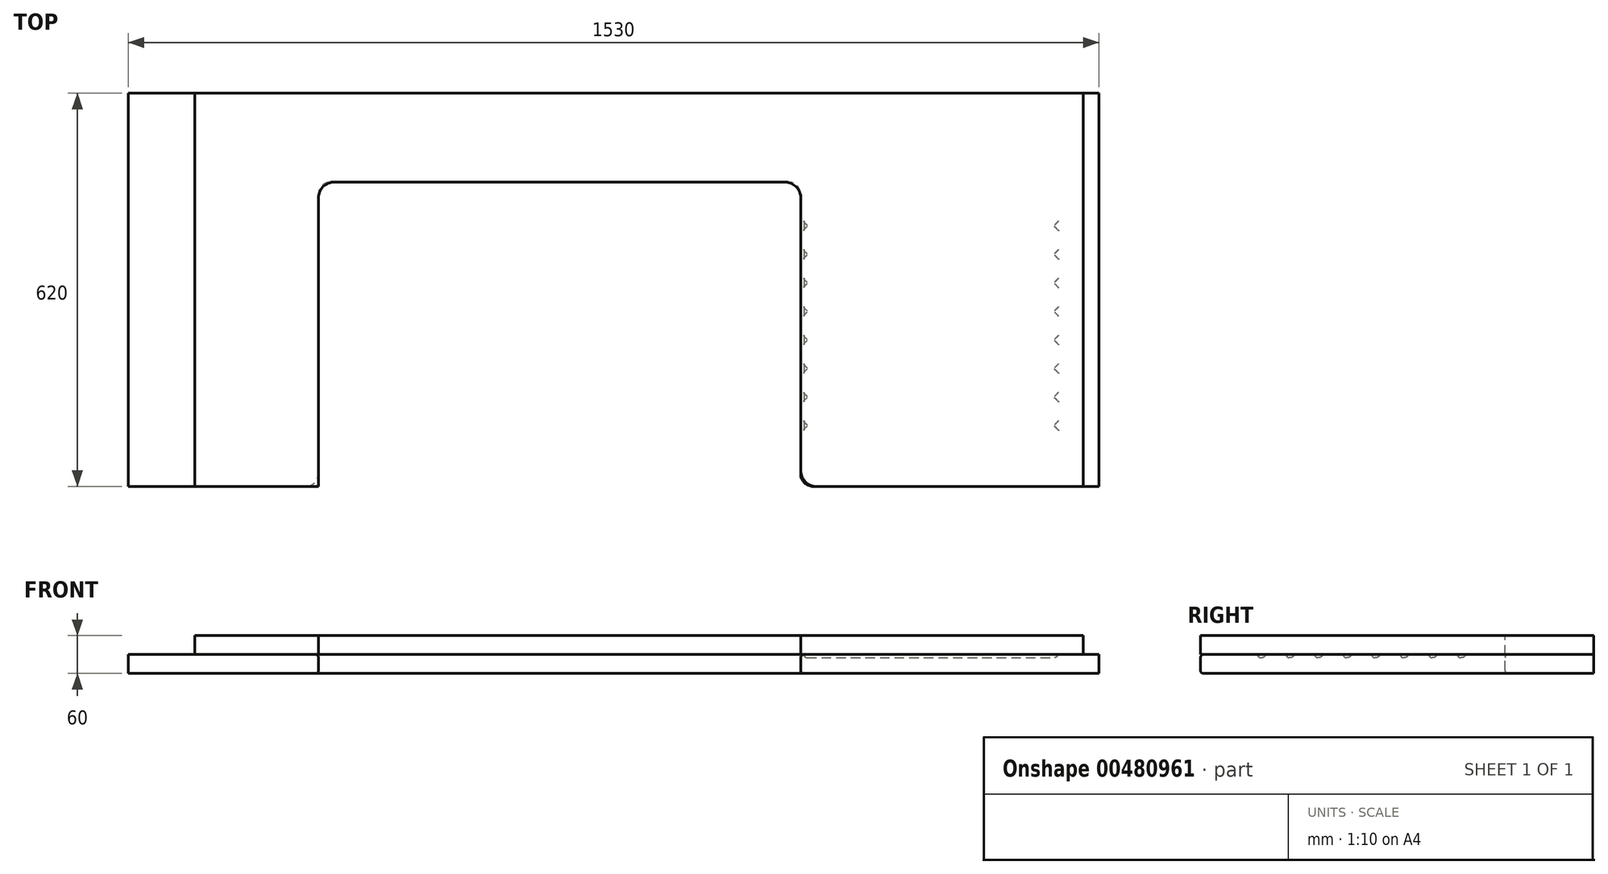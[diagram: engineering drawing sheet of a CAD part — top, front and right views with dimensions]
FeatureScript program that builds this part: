
annotation { "Feature Type Name" : "Feature", "Feature Type Description" : "" }
export const myFeature = defineFeature(function(context is Context, id is Id, definition is map)
    precondition{}
    {
        {
            var Q0;
            Q0=qCreatedBy(makeId("Top.planeOp"),FACE);
            var sketch = newSketch(context, id + "F0", { "sketchPlane" : qUnion([Q0])});
            skLineSegment(sketch, "E0.bottom", {"start": v(1945, 1810) * mm, "end": v(-1945, 1810) * mm});
            skLineSegment(sketch, "E0.top", {"start": v(1945, -1810) * mm, "end": v(-1945, -1810) * mm});
            skLineSegment(sketch, "E0.left", {"start": v(1945, 1810) * mm, "end": v(1945, -1810) * mm});
            skLineSegment(sketch, "E0.right", {"start": v(-1945, 1810) * mm, "end": v(-1945, -1810) * mm});
            skPoint(sketch, "E0.middle", {"position": v(0, 0) * mm});
            skLineSegment(sketch, "E1", {"start": v(1945, 1810) * mm, "end": v(1945, 45) * mm});
            skLineSegment(sketch, "E2.right", {"start": v(1945, 1810) * mm, "end": v(1945, 1158) * mm});
            skLineSegment(sketch, "E3.bottom", {"start": v(1945, 1810) * mm, "end": v(1285, 1810) * mm});
            skLineSegment(sketch, "E4.bottom", {"start": v(1945, 730) * mm, "end": v(1300, 730) * mm});
            skLineSegment(sketch, "E4.top", {"start": v(1945, 135) * mm, "end": v(1300, 135) * mm});
            skLineSegment(sketch, "E4.left", {"start": v(1945, 730) * mm, "end": v(1945, 135) * mm});
            skLineSegment(sketch, "E4.right", {"start": v(1300, 730) * mm, "end": v(1300, 135) * mm});
            skPoint(sketch, "E5.endSnap0", {"position": v(0, 1810) * mm});
            skLineSegment(sketch, "E6.bottom", {"start": v(-315, 1810) * mm, "end": v(485, 1810) * mm});
            skLineSegment(sketch, "E6.top", {"start": v(-315, 1250) * mm, "end": v(485, 1250) * mm});
            skLineSegment(sketch, "E6.left", {"start": v(-315, 1810) * mm, "end": v(-315, 1250) * mm});
            skLineSegment(sketch, "E6.right", {"start": v(485, 1810) * mm, "end": v(485, 1250) * mm});
            skLineSegment(sketch, "E7.bottom", {"start": v(485, 1810) * mm, "end": v(1085, 1810) * mm});
            skLineSegment(sketch, "E7.top", {"start": v(485, 1250) * mm, "end": v(1085, 1250) * mm});
            skLineSegment(sketch, "E7.right", {"start": v(1085, 1810) * mm, "end": v(1085, 1250) * mm});
            skLineSegment(sketch, "E8", {"start": v(1285, 1250) * mm, "end": v(1285, 780) * mm});
            skLineSegment(sketch, "E9", {"start": v(1285, 780) * mm, "end": v(1945, 780) * mm});
            skLineSegment(sketch, "E10", {"start": v(1285, 1250) * mm, "end": v(1285, 1810) * mm});
            skLineSegment(sketch, "E11", {"start": v(1285, 1680) * mm, "end": v(1845, 1680) * mm});
            skLineSegment(sketch, "E12.bottom", {"start": v(1285, 1250) * mm, "end": v(1215, 1250) * mm});
            skLineSegment(sketch, "E12.top", {"start": v(1285, 1810) * mm, "end": v(1215, 1810) * mm});
            skLineSegment(sketch, "E12.right", {"start": v(1215, 1250) * mm, "end": v(1215, 1810) * mm});
            skLineSegment(sketch, "E13.left", {"start": v(1215, 1810) * mm, "end": v(1215, 1250) * mm});
            skLineSegment(sketch, "E14", {"start": v(1215, 1250) * mm, "end": v(1085, 1250) * mm});
            skLineSegment(sketch, "E15.bottom", {"start": v(-315, 1250) * mm, "end": v(-715, 1250) * mm});
            skLineSegment(sketch, "E15.top", {"start": v(-315, 1810) * mm, "end": v(-715, 1810) * mm});
            skLineSegment(sketch, "E15.left", {"start": v(-315, 1250) * mm, "end": v(-315, 1810) * mm});
            skLineSegment(sketch, "E15.right", {"start": v(-715, 1250) * mm, "end": v(-715, 1810) * mm});
            skLineSegment(sketch, "E16.bottom", {"start": v(-1945, 1680) * mm, "end": v(-1385, 1680) * mm});
            skLineSegment(sketch, "E16.top", {"start": v(-1945, 680) * mm, "end": v(-1385, 680) * mm});
            skLineSegment(sketch, "E16.left", {"start": v(-1945, 1680) * mm, "end": v(-1945, 680) * mm});
            skLineSegment(sketch, "E16.right", {"start": v(-1385, 1680) * mm, "end": v(-1385, 680) * mm});
            skLineSegment(sketch, "E17.top", {"start": v(-1945, -220) * mm, "end": v(-1385, -220) * mm});
            skLineSegment(sketch, "E17.left", {"start": v(-1945, 680) * mm, "end": v(-1945, -220) * mm});
            skLineSegment(sketch, "E17.right", {"start": v(-1385, 680) * mm, "end": v(-1385, -220) * mm});
            skLineSegment(sketch, "E18.bottom", {"start": v(-1385, 1250) * mm, "end": v(-1315, 1250) * mm});
            skLineSegment(sketch, "E18.top", {"start": v(-1385, 1810) * mm, "end": v(-1315, 1810) * mm});
            skLineSegment(sketch, "E18.left", {"start": v(-1385, 1250) * mm, "end": v(-1385, 1810) * mm});
            skLineSegment(sketch, "E18.right", {"start": v(-1315, 1250) * mm, "end": v(-1315, 1810) * mm});
            skLineSegment(sketch, "E19.bottom", {"start": v(-715, 1250) * mm, "end": v(-1315, 1250) * mm});
            skLineSegment(sketch, "E19.top", {"start": v(-715, 1810) * mm, "end": v(-1315, 1810) * mm});
            skLineSegment(sketch, "E20.bottom", {"start": v(-1385, -220) * mm, "end": v(-1945, -220) * mm});
            skLineSegment(sketch, "E20.top", {"start": v(-1385, -1220) * mm, "end": v(-1945, -1220) * mm});
            skLineSegment(sketch, "E20.left", {"start": v(-1385, -220) * mm, "end": v(-1385, -1220) * mm});
            skLineSegment(sketch, "E20.right", {"start": v(-1945, -220) * mm, "end": v(-1945, -1220) * mm});
            skLineSegment(sketch, "E21.top", {"start": v(-1385, -1720) * mm, "end": v(-1945, -1720) * mm});
            skLineSegment(sketch, "E21.left", {"start": v(-1385, -1220) * mm, "end": v(-1385, -1720) * mm});
            skLineSegment(sketch, "E21.right", {"start": v(-1945, -1220) * mm, "end": v(-1945, -1720) * mm});
            skLineSegment(sketch, "E22.bottom", {"start": v(-385, 250) * mm, "end": v(175, 250) * mm});
            skLineSegment(sketch, "E22.top", {"start": v(-385, -650) * mm, "end": v(175, -650) * mm});
            skLineSegment(sketch, "E22.left", {"start": v(-385, 250) * mm, "end": v(-385, -650) * mm});
            skLineSegment(sketch, "E22.right", {"start": v(175, 250) * mm, "end": v(175, -650) * mm});
            skLineSegment(sketch, "E23.top", {"start": v(175, -260) * mm, "end": v(275, -260) * mm});
            skLineSegment(sketch, "E23.left", {"start": v(175, 250) * mm, "end": v(175, -260) * mm});
            skLineSegment(sketch, "E24.bottom", {"start": v(275, -260) * mm, "end": v(175, -260) * mm});
            skLineSegment(sketch, "E24.right", {"start": v(175, -260) * mm, "end": v(175, -650) * mm});
            skLineSegment(sketch, "E25.bottom", {"start": v(7324.8, -1561.68) * mm, "end": v(7884.8, -1561.68) * mm});
            skLineSegment(sketch, "E25.top", {"start": v(7324.8, -691.68) * mm, "end": v(7884.8, -691.68) * mm});
            skLineSegment(sketch, "E25.left", {"start": v(7324.8, -1561.68) * mm, "end": v(7324.8, -691.68) * mm});
            skLineSegment(sketch, "E25.right", {"start": v(7884.8, -1561.68) * mm, "end": v(7884.8, -691.68) * mm});
            skLineSegment(sketch, "E26.left", {"start": v(7324.8, -161.68) * mm, "end": v(7324.8, 738.32) * mm});
            skLineSegment(sketch, "E27", {"start": v(7324.8, -1561.68) * mm, "end": v(7324.8, 813.32) * mm});
            skPoint(sketch, "E26.top.end.orphan", {"position": v(7884.8, 608.32) * mm});
            skLineSegment(sketch, "E28.bottom", {"start": v(7324.8, -161.68) * mm, "end": v(7724.8, -161.68) * mm});
            skLineSegment(sketch, "E28.top", {"start": v(7324.8, 738.32) * mm, "end": v(7724.8, 738.32) * mm});
            skLineSegment(sketch, "E28.right", {"start": v(7724.8, -161.68) * mm, "end": v(7724.8, 738.32) * mm});
            skLineSegment(sketch, "E29", {"start": v(-1015, 1810) * mm, "end": v(-1015, 1589) * mm, "construction": true});
            skLineSegment(sketch, "E30.bottom", {"start": v(-310, 2102.18) * mm, "end": v(460, 2102.18) * mm});
            skLineSegment(sketch, "E30.top", {"start": v(-310, 1971.27) * mm, "end": v(460, 1971.27) * mm});
            skLineSegment(sketch, "E30.left", {"start": v(-310, 2102.18) * mm, "end": v(-310, 1971.27) * mm});
            skLineSegment(sketch, "E30.right", {"start": v(460, 2102.18) * mm, "end": v(460, 1971.27) * mm});
            skLineSegment(sketch, "E31.top", {"start": v(-310, 1810) * mm, "end": v(-1945, 1810) * mm});
            skLineSegment(sketch, "E32.bottom", {"start": v(485, 1810) * mm, "end": v(635, 1810) * mm});
            skLineSegment(sketch, "E32.top", {"start": v(485, 1250) * mm, "end": v(635, 1250) * mm});
            skLineSegment(sketch, "E33", {"start": v(1845, 1680) * mm, "end": v(1845, 780) * mm});
            skLineSegment(sketch, "E34.bottom", {"start": v(485, 1810) * mm, "end": v(562.5, 1810) * mm});
            skLineSegment(sketch, "E34.top", {"start": v(485, 1250) * mm, "end": v(785, 1250) * mm});
            skPoint(sketch, "E35.start.orphan", {"position": v(1150, 1250) * mm});
            skLineSegment(sketch, "E36.bottom", {"start": v(1085, 1810) * mm, "end": v(1185, 1810) * mm});
            skLineSegment(sketch, "E36.top", {"start": v(1085, 1250) * mm, "end": v(1185, 1250) * mm});
            skLineSegment(sketch, "E36.right", {"start": v(1185, 1810) * mm, "end": v(1185, 1250) * mm});
            skLineSegment(sketch, "E37", {"start": v(785, 1810) * mm, "end": v(785, 1670.24) * mm, "construction": true});
            skLineSegment(sketch, "E38.bottom", {"start": v(7324.8, -1411.68) * mm, "end": v(7884.8, -1411.68) * mm});
            skLineSegment(sketch, "E38.left", {"start": v(7324.8, -1411.68) * mm, "end": v(7324.8, -691.68) * mm});
            skLineSegment(sketch, "E38.right", {"start": v(7884.8, -1411.68) * mm, "end": v(7884.8, -691.68) * mm});
            skLineSegment(sketch, "E39.bottom", {"start": v(7324.8, -691.68) * mm, "end": v(7909.99, -691.68) * mm});
            skLineSegment(sketch, "E39.top", {"start": v(7324.8, -651.68) * mm, "end": v(7909.99, -651.68) * mm});
            skLineSegment(sketch, "E39.left", {"start": v(7324.8, -691.68) * mm, "end": v(7324.8, -651.68) * mm});
            skLineSegment(sketch, "E39.right", {"start": v(7909.99, -691.68) * mm, "end": v(7909.99, -651.68) * mm});
            skLineSegment(sketch, "E40.bottom", {"start": v(7884.8, -1411.68) * mm, "end": v(7324.8, -1411.68) * mm});
            skLineSegment(sketch, "E40.top", {"start": v(7884.8, -916.68) * mm, "end": v(7324.8, -916.68) * mm});
            skLineSegment(sketch, "E40.left", {"start": v(7884.8, -1411.68) * mm, "end": v(7884.8, -916.68) * mm});
            skLineSegment(sketch, "E40.right", {"start": v(7324.8, -1411.68) * mm, "end": v(7324.8, -916.68) * mm});
            skLineSegment(sketch, "E41.bottom", {"start": v(7324.8, -916.68) * mm, "end": v(7884.8, -916.68) * mm});
            skLineSegment(sketch, "E41.top", {"start": v(7324.8, -716.68) * mm, "end": v(7884.8, -716.68) * mm});
            skLineSegment(sketch, "E41.left", {"start": v(7324.8, -916.68) * mm, "end": v(7324.8, -716.68) * mm});
            skLineSegment(sketch, "E41.right", {"start": v(7884.8, -916.68) * mm, "end": v(7884.8, -716.68) * mm});
            skLineSegment(sketch, "E42.left", {"start": v(-385, 250) * mm, "end": v(-385, 269) * mm});
            skLineSegment(sketch, "E43.top", {"start": v(1285, 761) * mm, "end": v(1945, 761) * mm});
            skLineSegment(sketch, "E43.left", {"start": v(1285, 780) * mm, "end": v(1285, 761) * mm});
            skLineSegment(sketch, "E43.right", {"start": v(1945, 780) * mm, "end": v(1945, 761) * mm});
            skLineSegment(sketch, "E44.bottom", {"start": v(-1945, -1720) * mm, "end": v(-1385, -1720) * mm});
            skLineSegment(sketch, "E44.left", {"start": v(-1945, -1720) * mm, "end": v(-1945, -1739) * mm});
            skLineSegment(sketch, "E45.bottom", {"start": v(-385, 250) * mm, "end": v(-285, 250) * mm});
            skLineSegment(sketch, "E45.top", {"start": v(-355, 300) * mm, "end": v(-285, 300) * mm});
            skLineSegment(sketch, "E45.left", {"start": v(-385, 250) * mm, "end": v(-385, 270) * mm});
            skLineSegment(sketch, "E45.right", {"start": v(-285, 250) * mm, "end": v(-285, 300) * mm});
            skPoint(sketch, "E46.visualSharp", {"position": v(-385, 300) * mm});
            skArc(sketch, "E46.filletArc", {"start": v(-355, 300) * mm, "mid": v(-376.21, 291.21) * mm, "end": v(-385, 270) * mm});
            skLineSegment(sketch, "E47.left", {"start": v(-285, 300) * mm, "end": v(-285, 281) * mm});
            skPoint(sketch, "E47.right.end.orphan", {"position": v(344, 281) * mm});
            skLineSegment(sketch, "E48.bottom", {"start": v(-285, 300) * mm, "end": v(175, 300) * mm});
            skLineSegment(sketch, "E48.top", {"start": v(-285, 281) * mm, "end": v(175, 281) * mm});
            skLineSegment(sketch, "E48.right", {"start": v(175, 300) * mm, "end": v(175, 281) * mm});
            skLineSegment(sketch, "E49", {"start": v(175, 250) * mm, "end": v(175, 300) * mm});
            skPoint(sketch, "E50.right.start.orphan", {"position": v(344, 269) * mm});
            skPoint(sketch, "E51.end.orphan", {"position": v(275, -264.2) * mm});
            skPoint(sketch, "E51.start.orphan", {"position": v(275, 300) * mm});
            skLineSegment(sketch, "E52.bottom", {"start": v(175, 300) * mm, "end": v(275, 300) * mm});
            skLineSegment(sketch, "E52.left", {"start": v(175, 300) * mm, "end": v(175, -260) * mm});
            skLineSegment(sketch, "E52.right", {"start": v(275, 300) * mm, "end": v(275, -260) * mm});
            skLineSegment(sketch, "E53.bottom", {"start": v(-385, -650) * mm, "end": v(-285, -650) * mm});
            skLineSegment(sketch, "E53.top", {"start": v(-355, -700) * mm, "end": v(-285, -700) * mm});
            skLineSegment(sketch, "E53.left", {"start": v(-385, -650) * mm, "end": v(-385, -670) * mm});
            skLineSegment(sketch, "E53.right", {"start": v(-285, -650) * mm, "end": v(-285, -700) * mm});
            skPoint(sketch, "E54.visualSharp", {"position": v(-385, -700) * mm});
            skArc(sketch, "E54.filletArc", {"start": v(-385, -670) * mm, "mid": v(-376.21, -691.21) * mm, "end": v(-355, -700) * mm});
            skLineSegment(sketch, "E55.bottom", {"start": v(-285, -700) * mm, "end": v(275, -700) * mm});
            skLineSegment(sketch, "E55.top", {"start": v(-285, -681) * mm, "end": v(175, -681) * mm});
            skLineSegment(sketch, "E55.left", {"start": v(-285, -700) * mm, "end": v(-285, -681) * mm});
            skLineSegment(sketch, "E55.right", {"start": v(275, -700) * mm, "end": v(275, -681) * mm});
            skLineSegment(sketch, "E56.top", {"start": v(275, -700) * mm, "end": v(175, -700) * mm});
            skLineSegment(sketch, "E56.left", {"start": v(275, -260) * mm, "end": v(275, -700) * mm});
            skLineSegment(sketch, "E56.right", {"start": v(175, -260) * mm, "end": v(175, -700) * mm});
            skLineSegment(sketch, "E57.bottom", {"start": v(275, 300) * mm, "end": v(294, 300) * mm});
            skLineSegment(sketch, "E57.top", {"start": v(275, -700) * mm, "end": v(294, -700) * mm});
            skLineSegment(sketch, "E57.left", {"start": v(275, 300) * mm, "end": v(275, -700) * mm});
            skLineSegment(sketch, "E57.right", {"start": v(294, 300) * mm, "end": v(294, -700) * mm});
            skLineSegment(sketch, "E58.bottom", {"start": v(-1945, -1770) * mm, "end": v(-1485, -1770) * mm});
            skLineSegment(sketch, "E58.top", {"start": v(-1945, -1751) * mm, "end": v(-1485, -1751) * mm});
            skLineSegment(sketch, "E58.left", {"start": v(-1945, -1770) * mm, "end": v(-1945, -1751) * mm});
            skLineSegment(sketch, "E58.right", {"start": v(-1485, -1770) * mm, "end": v(-1485, -1751) * mm});
            skLineSegment(sketch, "E59.bottom", {"start": v(-1385, -1720) * mm, "end": v(-1485, -1720) * mm});
            skLineSegment(sketch, "E59.top", {"start": v(-1415, -1770) * mm, "end": v(-1485, -1770) * mm});
            skLineSegment(sketch, "E59.left", {"start": v(-1385, -1720) * mm, "end": v(-1385, -1740) * mm});
            skLineSegment(sketch, "E59.right", {"start": v(-1485, -1720) * mm, "end": v(-1485, -1770) * mm});
            skPoint(sketch, "E60.visualSharp", {"position": v(-1385, -1770) * mm});
            skArc(sketch, "E60.filletArc", {"start": v(-1415, -1770) * mm, "mid": v(-1393.79, -1761.21) * mm, "end": v(-1385, -1740) * mm});
            skLineSegment(sketch, "E61.left", {"start": v(7324.8, 738.32) * mm, "end": v(7324.8, 378.32) * mm});
            skLineSegment(sketch, "E61.right", {"start": v(7724.8, 738.32) * mm, "end": v(7724.8, 288.32) * mm});
            skLineSegment(sketch, "E62.left", {"start": v(7724.8, -191.68) * mm, "end": v(7724.8, 508.32) * mm});
            skLineSegment(sketch, "E62.right", {"start": v(7324.8, -191.68) * mm, "end": v(7324.8, 508.32) * mm});
            skLineSegment(sketch, "E63", {"start": v(-1945, 230) * mm, "end": v(-1763.05, 230) * mm});
            skLineSegment(sketch, "E64.bottom", {"start": v(7324.8, -136.68) * mm, "end": v(7689.8, -136.68) * mm});
            skLineSegment(sketch, "E64.top", {"start": v(7324.8, 623.32) * mm, "end": v(7689.8, 623.32) * mm});
            skLineSegment(sketch, "E64.left", {"start": v(7324.8, -136.68) * mm, "end": v(7324.8, 623.32) * mm});
            skLineSegment(sketch, "E64.right", {"start": v(7689.8, -136.68) * mm, "end": v(7689.8, 623.32) * mm});
            skPoint(sketch, "E65.oppositeSnap0", {"position": v(7507.3, 623.32) * mm});
            skLineSegment(sketch, "E65.bottom", {"start": v(7407.3, 623.32) * mm, "end": v(7507.3, 623.32) * mm});
            skLineSegment(sketch, "E65.top", {"start": v(7407.3, 723.32) * mm, "end": v(7507.3, 723.32) * mm});
            skLineSegment(sketch, "E65.left", {"start": v(7407.3, 623.32) * mm, "end": v(7407.3, 723.32) * mm});
            skLineSegment(sketch, "E65.right", {"start": v(7507.3, 623.32) * mm, "end": v(7507.3, 723.32) * mm});
            skSolve(sketch);
        }
        {
            var Q0;
            Q0=qCreatedBy(makeId("Top.planeOp"),FACE);
            var sketch = newSketch(context, id + "F1", { "sketchPlane" : qUnion([Q0])});
            skLineSegment(sketch, "E66.bottom", {"start": v(1945, 1810) * mm, "end": v(1845, 1810) * mm});
            skLineSegment(sketch, "E66.top", {"start": v(1945, 780) * mm, "end": v(1845, 780) * mm});
            skLineSegment(sketch, "E66.left", {"start": v(1945, 1810) * mm, "end": v(1945, 780) * mm});
            skLineSegment(sketch, "E67", {"start": v(1845, 780) * mm, "end": v(1845, 1810) * mm});
            skLineSegment(sketch, "E68", {"start": v(1845, 1810) * mm, "end": v(1235, 1810) * mm});
            skLineSegment(sketch, "E69", {"start": v(1235, 1810) * mm, "end": v(1235, 1510) * mm});
            skLineSegment(sketch, "E70", {"start": v(1235, 1510) * mm, "end": v(1235, 1510) * mm});
            skLineSegment(sketch, "E71", {"start": v(1545, 1510) * mm, "end": v(1545, 1510) * mm});
            skLineSegment(sketch, "E72", {"start": v(1545, 1510) * mm, "end": v(1845, 1510) * mm});
            skLineSegment(sketch, "E73.bottom", {"start": v(1845, 1510) * mm, "end": v(1545, 1510) * mm});
            skLineSegment(sketch, "E73.top", {"start": v(1845, 1480) * mm, "end": v(1545, 1480) * mm});
            skLineSegment(sketch, "E73.left", {"start": v(1845, 1510) * mm, "end": v(1845, 1480) * mm});
            skLineSegment(sketch, "E73.right", {"start": v(1545, 1510) * mm, "end": v(1545, 1480) * mm});
            skLineSegment(sketch, "E74.bottom", {"start": v(1235, 1810) * mm, "end": v(635, 1810) * mm});
            skLineSegment(sketch, "E74.top", {"start": v(1235, 1510) * mm, "end": v(635, 1510) * mm});
            skLineSegment(sketch, "E74.right", {"start": v(635, 1810) * mm, "end": v(635, 1510) * mm});
            skLineSegment(sketch, "E75.bottom", {"start": v(1235, 1810) * mm, "end": v(970, 1810) * mm});
            skLineSegment(sketch, "E75.top", {"start": v(1235, 1510) * mm, "end": v(970, 1510) * mm});
            skLineSegment(sketch, "E76.bottom", {"start": v(-495, 1810) * mm, "end": v(-1215, 1810) * mm});
            skLineSegment(sketch, "E76.top", {"start": v(-495, 1510) * mm, "end": v(-1215, 1510) * mm});
            skLineSegment(sketch, "E76.left", {"start": v(-495, 1810) * mm, "end": v(-495, 1510) * mm});
            skLineSegment(sketch, "E76.right", {"start": v(-1215, 1810) * mm, "end": v(-1215, 1510) * mm});
            skLineSegment(sketch, "E77.bottom", {"start": v(-495, 1810) * mm, "end": v(-795, 1810) * mm});
            skLineSegment(sketch, "E77.top", {"start": v(-495, 1510) * mm, "end": v(-795, 1510) * mm});
            skLineSegment(sketch, "E77.right", {"start": v(-795, 1810) * mm, "end": v(-795, 1510) * mm});
            skLineSegment(sketch, "E78", {"start": v(-1945, 1810) * mm, "end": v(-1215, 1810) * mm});
            skLineSegment(sketch, "E79", {"start": v(-1945, 1510) * mm, "end": v(-1945, 1810) * mm});
            skLineSegment(sketch, "E80.left", {"start": v(-1945, 1510) * mm, "end": v(-1945, 1500) * mm});
            skLineSegment(sketch, "E80.right", {"start": v(-1645, 1510) * mm, "end": v(-1645, 1500) * mm});
            skLineSegment(sketch, "E81.bottom", {"start": v(-1944.69, -220) * mm, "end": v(-1645, -220) * mm});
            skLineSegment(sketch, "E81.top", {"start": v(-1944.69, -1220) * mm, "end": v(-1645, -1220) * mm});
            skLineSegment(sketch, "E81.left", {"start": v(-1944.69, -220) * mm, "end": v(-1944.69, -1220) * mm});
            skLineSegment(sketch, "E81.right", {"start": v(-1645, -220) * mm, "end": v(-1645, -1220) * mm});
            skLineSegment(sketch, "E82.bottom", {"start": v(-1645, -1220) * mm, "end": v(-1945, -1220) * mm});
            skLineSegment(sketch, "E82.top", {"start": v(-1645, -1720) * mm, "end": v(-1945, -1720) * mm});
            skLineSegment(sketch, "E82.left", {"start": v(-1645, -1220) * mm, "end": v(-1645, -1720) * mm});
            skLineSegment(sketch, "E82.right", {"start": v(-1945, -1220) * mm, "end": v(-1945, -1720) * mm});
            skLineSegment(sketch, "E83", {"start": v(-1215, 1510) * mm, "end": v(-1945, 1510) * mm});
            skLineSegment(sketch, "E84", {"start": v(1845, 1495) * mm, "end": v(1727.18, 1495) * mm, "construction": true});
            skPoint(sketch, "E84.endSnap0", {"position": v(1845, 1495) * mm});
            skLineSegment(sketch, "E85", {"start": v(1235, 1510) * mm, "end": v(1845, 1510) * mm});
            skLineSegment(sketch, "E86", {"start": v(-1195, 1510) * mm, "end": v(-1195, 1810) * mm});
            skLineSegment(sketch, "E87.bottom", {"start": v(-495, 1510) * mm, "end": v(-476, 1510) * mm});
            skLineSegment(sketch, "E87.top", {"start": v(-495, 1810) * mm, "end": v(-476, 1810) * mm});
            skLineSegment(sketch, "E87.left", {"start": v(-495, 1510) * mm, "end": v(-495, 1810) * mm});
            skLineSegment(sketch, "E87.right", {"start": v(-476, 1510) * mm, "end": v(-476, 1810) * mm});
            skLineSegment(sketch, "E88.bottom", {"start": v(635, 1510) * mm, "end": v(616, 1510) * mm});
            skLineSegment(sketch, "E88.top", {"start": v(635, 1810) * mm, "end": v(616, 1810) * mm});
            skLineSegment(sketch, "E88.left", {"start": v(635, 1510) * mm, "end": v(635, 1810) * mm});
            skLineSegment(sketch, "E88.right", {"start": v(616, 1510) * mm, "end": v(616, 1810) * mm});
            skLineSegment(sketch, "E89", {"start": v(-1945, 1500) * mm, "end": v(-1645, 1500) * mm});
            skLineSegment(sketch, "E90.left", {"start": v(-1945, 1500) * mm, "end": v(-1945, 1500) * mm});
            skLineSegment(sketch, "E90.right", {"start": v(-1645, 1500) * mm, "end": v(-1645, 1500) * mm});
            skLineSegment(sketch, "E91.bottom", {"start": v(1545, 1480) * mm, "end": v(1845, 1480) * mm});
            skLineSegment(sketch, "E91.top", {"start": v(1545, 880) * mm, "end": v(1845, 880) * mm});
            skLineSegment(sketch, "E91.left", {"start": v(1545, 1480) * mm, "end": v(1545, 880) * mm});
            skLineSegment(sketch, "E91.right", {"start": v(1845, 1480) * mm, "end": v(1845, 880) * mm});
            skLineSegment(sketch, "E92.top", {"start": v(-1945, 700) * mm, "end": v(-1645, 700) * mm});
            skLineSegment(sketch, "E92.left", {"start": v(-1945, 1500) * mm, "end": v(-1945, 700) * mm});
            skLineSegment(sketch, "E92.right", {"start": v(-1645, 1500) * mm, "end": v(-1645, 700) * mm});
            skLineSegment(sketch, "E93.bottom", {"start": v(-1945, 1810) * mm, "end": v(-1915, 1810) * mm});
            skLineSegment(sketch, "E93.top", {"start": v(-1945, 1510) * mm, "end": v(-1915, 1510) * mm});
            skLineSegment(sketch, "E93.left", {"start": v(-1945, 1810) * mm, "end": v(-1945, 1510) * mm});
            skLineSegment(sketch, "E93.right", {"start": v(-1915, 1810) * mm, "end": v(-1915, 1510) * mm});
            skLineSegment(sketch, "E94.bottom", {"start": v(1845, 1810) * mm, "end": v(1835, 1810) * mm});
            skLineSegment(sketch, "E94.top", {"start": v(1845, 1510) * mm, "end": v(1835, 1510) * mm});
            skLineSegment(sketch, "E94.left", {"start": v(1845, 1810) * mm, "end": v(1845, 1510) * mm});
            skLineSegment(sketch, "E94.right", {"start": v(1835, 1810) * mm, "end": v(1835, 1510) * mm});
            skSolve(sketch);
        }
        {
            var Q0;
            Q0=qCreatedBy(makeId("Top.planeOp"),FACE);
            var sketch = newSketch(context, id + "F2", { "sketchPlane" : qUnion([Q0])});
            skLineSegment(sketch, "E95.bottom", {"start": v(-415, 330) * mm, "end": v(324, 330) * mm});
            skLineSegment(sketch, "E95.top", {"start": v(-415, -730) * mm, "end": v(324, -730) * mm});
            skLineSegment(sketch, "E95.left", {"start": v(-415, 330) * mm, "end": v(-415, -730) * mm});
            skLineSegment(sketch, "E95.right", {"start": v(324, 330) * mm, "end": v(324, -730) * mm});
            skLineSegment(sketch, "E96", {"start": v(-1944.69, -1790) * mm, "end": v(-1324.69, -1790) * mm});
            skLineSegment(sketch, "E97", {"start": v(-1324.69, -1790) * mm, "end": v(-1324.69, -220) * mm});
            skLineSegment(sketch, "E98", {"start": v(-1324.69, -220) * mm, "end": v(-1944.69, -220) * mm});
            skLineSegment(sketch, "E99", {"start": v(-1944.69, -220) * mm, "end": v(-1944.69, -1790) * mm});
            skLineSegment(sketch, "E100", {"start": v(-1945, 680) * mm, "end": v(-1325, 680) * mm});
            skLineSegment(sketch, "E101", {"start": v(-1325, 680) * mm, "end": v(-1325, 1190) * mm});
            skLineSegment(sketch, "E102", {"start": v(-1325, 1190) * mm, "end": v(-490, 1190) * mm});
            skLineSegment(sketch, "E103", {"start": v(-490, 1190) * mm, "end": v(-490, 1810) * mm});
            skLineSegment(sketch, "E104", {"start": v(-490, 1810) * mm, "end": v(-1945, 1810) * mm});
            skLineSegment(sketch, "E105", {"start": v(-1945, 1810) * mm, "end": v(-1945, 680) * mm});
            skLineSegment(sketch, "E106", {"start": v(910, 1810) * mm, "end": v(910, 1190) * mm});
            skLineSegment(sketch, "E107", {"start": v(910, 1190) * mm, "end": v(1225, 1190) * mm});
            skLineSegment(sketch, "E108", {"start": v(1225, 1190) * mm, "end": v(1225, 731) * mm});
            skLineSegment(sketch, "E109", {"start": v(1225, 731) * mm, "end": v(1945, 731) * mm});
            skLineSegment(sketch, "E110", {"start": v(1945, 731) * mm, "end": v(1945, 1810) * mm});
            skLineSegment(sketch, "E111", {"start": v(1945, 1810) * mm, "end": v(910, 1810) * mm});
            skSolve(sketch);
        }
        {
            var Q0;
            Q0=qCreatedBy(makeId("Top.planeOp"),FACE);
            var sketch = newSketch(context, id + "F3", { "sketchPlane" : qUnion([Q0])});
            skLineSegment(sketch, "E112.bottom", {"start": v(-595, 1810) * mm, "end": v(935, 1810) * mm});
            skLineSegment(sketch, "E112.top", {"start": v(-595, 1190) * mm, "end": v(-315, 1190) * mm});
            skLineSegment(sketch, "E112.left", {"start": v(-595, 1810) * mm, "end": v(-595, 1190) * mm});
            skLineSegment(sketch, "E112.right", {"start": v(935, 1810) * mm, "end": v(935, 1190) * mm});
            skLineSegment(sketch, "E113.bottom", {"start": v(-275, 1670) * mm, "end": v(445, 1670) * mm});
            skLineSegment(sketch, "E113.left", {"start": v(-295, 1650) * mm, "end": v(-295, 1210) * mm});
            skLineSegment(sketch, "E113.right", {"start": v(465, 1650) * mm, "end": v(465, 1210) * mm});
            skLineSegment(sketch, "E114.trimOffspring", {"start": v(485, 1190) * mm, "end": v(935, 1190) * mm});
            skPoint(sketch, "E115.visualSharp", {"position": v(-295, 1190) * mm});
            skArc(sketch, "E115.filletArc", {"start": v(-315, 1190) * mm, "mid": v(-300.86, 1195.86) * mm, "end": v(-295, 1210) * mm});
            skPoint(sketch, "E116.visualSharp", {"position": v(465, 1190) * mm});
            skArc(sketch, "E116.filletArc", {"start": v(465, 1210) * mm, "mid": v(470.86, 1195.86) * mm, "end": v(485, 1190) * mm});
            skPoint(sketch, "E117.visualSharp", {"position": v(-295, 1670) * mm});
            skArc(sketch, "E117.filletArc", {"start": v(-275, 1670) * mm, "mid": v(-289.14, 1664.14) * mm, "end": v(-295, 1650) * mm});
            skPoint(sketch, "E118.visualSharp", {"position": v(465, 1670) * mm});
            skArc(sketch, "E118.filletArc", {"start": v(465, 1650) * mm, "mid": v(459.14, 1664.14) * mm, "end": v(445, 1670) * mm});
            skSolve(sketch);
        }
        {
            var Q0;
            Q0 = qSketchRegion(id + "F3", true);
            extrude(context, id + "F4", {"entities" : qUnion([Q0]), "oppositeDirection" : true, "depth" : 30 * mm, "offsetDistance" : 25 * mm});
        }
        {
            var Q0;
            Q0=makeQuery(id+"F4.opExtrude","CAP_EDGE",EDGE,{"disambiguationData":[OSD([sQuery(id+"F3.wireOp",EDGE,"E113.bottom")])],"isStart":true});
            var Q1;
            Q1=makeQuery(id+"F4.opExtrude","CAP_EDGE",EDGE,{"disambiguationData":[OSD([sQuery(id+"F3.wireOp",EDGE,"E114.trimOffspring")])],"isStart":false});
            fillet(context, id + "F5", {"entities" : qUnion([Q0, Q1]), "radius" : 5 * mm, "tangentPropagation" : true, "allowEdgeOverflow" : false});
        }
        {
            var Q0;
            Q0=makeQuery(id+"F4.opExtrude","CAP_FACE",FACE,{"disambiguationData":[OSD([sQuery(id+"F3.wireOp",EDGE,"E112.bottom"),sQuery(id+"F3.wireOp",EDGE,"E112.top"),sQuery(id+"F3.wireOp",EDGE,"E112.left"),sQuery(id+"F3.wireOp",EDGE,"E112.right"),sQuery(id+"F3.wireOp",EDGE,"E113.bottom"),sQuery(id+"F3.wireOp",EDGE,"E113.left"),sQuery(id+"F3.wireOp",EDGE,"E113.right"),sQuery(id+"F3.wireOp",EDGE,"E114.trimOffspring"),sQuery(id+"F3.wireOp",EDGE,"E115.filletArc"),sQuery(id+"F3.wireOp",EDGE,"E116.filletArc"),sQuery(id+"F3.wireOp",EDGE,"E117.filletArc"),sQuery(id+"F3.wireOp",EDGE,"E118.filletArc")])],"isStart":true});
            var sketch = newSketch(context, id + "F6", { "sketchPlane" : qUnion([Q0])});
            skLineSegment(sketch, "E119.bottom", {"start": v(470, 1280) * mm, "end": v(870, 1280) * mm});
            skLineSegment(sketch, "E119.top", {"start": v(470, 1292) * mm, "end": v(870, 1292) * mm});
            skLineSegment(sketch, "E119.left", {"start": v(470, 1280) * mm, "end": v(470, 1292) * mm});
            skLineSegment(sketch, "E119.right", {"start": v(870, 1280) * mm, "end": v(870, 1292) * mm});
            skLineSegment(sketch, "E120.0.1.0", {"start": v(470, 1337) * mm, "end": v(870, 1337) * mm});
            skLineSegment(sketch, "E120.0.1.1", {"start": v(470, 1325) * mm, "end": v(870, 1325) * mm});
            skLineSegment(sketch, "E120.0.1.2", {"start": v(870, 1325) * mm, "end": v(870, 1337) * mm});
            skLineSegment(sketch, "E120.0.1.3", {"start": v(470, 1325) * mm, "end": v(470, 1337) * mm});
            skLineSegment(sketch, "E120.0.2.0", {"start": v(470, 1382) * mm, "end": v(870, 1382) * mm});
            skLineSegment(sketch, "E120.0.2.1", {"start": v(470, 1370) * mm, "end": v(870, 1370) * mm});
            skLineSegment(sketch, "E120.0.2.2", {"start": v(870, 1370) * mm, "end": v(870, 1382) * mm});
            skLineSegment(sketch, "E120.0.2.3", {"start": v(470, 1370) * mm, "end": v(470, 1382) * mm});
            skLineSegment(sketch, "E120.0.3.0", {"start": v(470, 1427) * mm, "end": v(870, 1427) * mm});
            skLineSegment(sketch, "E120.0.3.1", {"start": v(470, 1415) * mm, "end": v(870, 1415) * mm});
            skLineSegment(sketch, "E120.0.3.2", {"start": v(870, 1415) * mm, "end": v(870, 1427) * mm});
            skLineSegment(sketch, "E120.0.3.3", {"start": v(470, 1415) * mm, "end": v(470, 1427) * mm});
            skLineSegment(sketch, "E120.0.4.0", {"start": v(470, 1472) * mm, "end": v(870, 1472) * mm});
            skLineSegment(sketch, "E120.0.4.1", {"start": v(470, 1460) * mm, "end": v(870, 1460) * mm});
            skLineSegment(sketch, "E120.0.4.2", {"start": v(870, 1460) * mm, "end": v(870, 1472) * mm});
            skLineSegment(sketch, "E120.0.4.3", {"start": v(470, 1460) * mm, "end": v(470, 1472) * mm});
            skLineSegment(sketch, "E120.0.5.0", {"start": v(470, 1517) * mm, "end": v(870, 1517) * mm});
            skLineSegment(sketch, "E120.0.5.1", {"start": v(470, 1505) * mm, "end": v(870, 1505) * mm});
            skLineSegment(sketch, "E120.0.5.2", {"start": v(870, 1505) * mm, "end": v(870, 1517) * mm});
            skLineSegment(sketch, "E120.0.5.3", {"start": v(470, 1505) * mm, "end": v(470, 1517) * mm});
            skLineSegment(sketch, "E120.0.6.0", {"start": v(470, 1562) * mm, "end": v(870, 1562) * mm});
            skLineSegment(sketch, "E120.0.6.1", {"start": v(470, 1550) * mm, "end": v(870, 1550) * mm});
            skLineSegment(sketch, "E120.0.6.2", {"start": v(870, 1550) * mm, "end": v(870, 1562) * mm});
            skLineSegment(sketch, "E120.0.6.3", {"start": v(470, 1550) * mm, "end": v(470, 1562) * mm});
            skLineSegment(sketch, "E120.0.7.0", {"start": v(470, 1607) * mm, "end": v(870, 1607) * mm});
            skLineSegment(sketch, "E120.0.7.1", {"start": v(470, 1595) * mm, "end": v(870, 1595) * mm});
            skLineSegment(sketch, "E120.0.7.2", {"start": v(870, 1595) * mm, "end": v(870, 1607) * mm});
            skLineSegment(sketch, "E120.0.7.3", {"start": v(470, 1595) * mm, "end": v(470, 1607) * mm});
            skLineSegment(sketch, "E120.direction1", {"start": v(470, 1292) * mm, "end": v(495, 1292) * mm, "construction": true});
            skLineSegment(sketch, "E120.direction2", {"start": v(470, 1292) * mm, "end": v(470, 1337) * mm, "construction": true});
            skSolve(sketch);
        }
        {
            var Q0;
            Q0 = qSketchRegion(id + "F6", true);
            extrude(context, id + "F7", {"entities" : qUnion([Q0]), "operationType" : NewBodyOperationType.REMOVE, "oppositeDirection" : true, "depth" : 5 * mm, "offsetDistance" : 25 * mm});
        }
        {
            var Q0;
            Q0=makeQuery(id+"F7.boolean.opBoolean","COPY",FACE,{"derivedFrom":makeQuery(id+"F7.opExtrude","CAP_FACE",FACE,{"disambiguationData":[OSD([sQuery(id+"F6.wireOp",EDGE,"E120.0.7.0"),sQuery(id+"F6.wireOp",EDGE,"E120.0.7.1"),sQuery(id+"F6.wireOp",EDGE,"E120.0.7.2"),sQuery(id+"F6.wireOp",EDGE,"E120.0.7.3")])],"isStart":false})});
            var Q1;
            Q1=makeQuery(id+"F7.boolean.opBoolean","COPY",FACE,{"derivedFrom":makeQuery(id+"F7.opExtrude","CAP_FACE",FACE,{"disambiguationData":[OSD([sQuery(id+"F6.wireOp",EDGE,"E120.0.6.0"),sQuery(id+"F6.wireOp",EDGE,"E120.0.6.1"),sQuery(id+"F6.wireOp",EDGE,"E120.0.6.2"),sQuery(id+"F6.wireOp",EDGE,"E120.0.6.3")])],"isStart":false})});
            var Q2;
            Q2=makeQuery(id+"F7.boolean.opBoolean","COPY",FACE,{"derivedFrom":makeQuery(id+"F7.opExtrude","CAP_FACE",FACE,{"disambiguationData":[OSD([sQuery(id+"F6.wireOp",EDGE,"E120.0.5.0"),sQuery(id+"F6.wireOp",EDGE,"E120.0.5.1"),sQuery(id+"F6.wireOp",EDGE,"E120.0.5.2"),sQuery(id+"F6.wireOp",EDGE,"E120.0.5.3")])],"isStart":false})});
            var Q3;
            Q3=makeQuery(id+"F7.boolean.opBoolean","COPY",FACE,{"derivedFrom":makeQuery(id+"F7.opExtrude","CAP_FACE",FACE,{"disambiguationData":[OSD([sQuery(id+"F6.wireOp",EDGE,"E120.0.4.0"),sQuery(id+"F6.wireOp",EDGE,"E120.0.4.1"),sQuery(id+"F6.wireOp",EDGE,"E120.0.4.2"),sQuery(id+"F6.wireOp",EDGE,"E120.0.4.3")])],"isStart":false})});
            var Q4;
            Q4=makeQuery(id+"F7.boolean.opBoolean","COPY",FACE,{"derivedFrom":makeQuery(id+"F7.opExtrude","CAP_FACE",FACE,{"disambiguationData":[OSD([sQuery(id+"F6.wireOp",EDGE,"E120.0.3.0"),sQuery(id+"F6.wireOp",EDGE,"E120.0.3.1"),sQuery(id+"F6.wireOp",EDGE,"E120.0.3.2"),sQuery(id+"F6.wireOp",EDGE,"E120.0.3.3")])],"isStart":false})});
            var Q5;
            Q5=makeQuery(id+"F7.boolean.opBoolean","COPY",FACE,{"derivedFrom":makeQuery(id+"F7.opExtrude","CAP_FACE",FACE,{"disambiguationData":[OSD([sQuery(id+"F6.wireOp",EDGE,"E120.0.2.0"),sQuery(id+"F6.wireOp",EDGE,"E120.0.2.1"),sQuery(id+"F6.wireOp",EDGE,"E120.0.2.2"),sQuery(id+"F6.wireOp",EDGE,"E120.0.2.3")])],"isStart":false})});
            var Q6;
            Q6=makeQuery(id+"F7.boolean.opBoolean","COPY",FACE,{"derivedFrom":makeQuery(id+"F7.opExtrude","CAP_FACE",FACE,{"disambiguationData":[OSD([sQuery(id+"F6.wireOp",EDGE,"E119.bottom"),sQuery(id+"F6.wireOp",EDGE,"E119.top"),sQuery(id+"F6.wireOp",EDGE,"E119.left"),sQuery(id+"F6.wireOp",EDGE,"E119.right")])],"isStart":false})});
            var Q7;
            Q7=makeQuery(id+"F7.boolean.opBoolean","COPY",FACE,{"derivedFrom":makeQuery(id+"F7.opExtrude","CAP_FACE",FACE,{"disambiguationData":[OSD([sQuery(id+"F6.wireOp",EDGE,"E120.0.1.0"),sQuery(id+"F6.wireOp",EDGE,"E120.0.1.1"),sQuery(id+"F6.wireOp",EDGE,"E120.0.1.2"),sQuery(id+"F6.wireOp",EDGE,"E120.0.1.3")])],"isStart":false})});
            fillet(context, id + "F8", {"entities" : qUnion([Q0, Q1, Q2, Q3, Q4, Q5, Q6, Q7]), "radius" : 5 * mm, "tangentPropagation" : true, "allowEdgeOverflow" : false});
        }
        {
            var Q0;
            Q0=makeQuery(id+"F8.opFillet","BLEND_EDGE",EDGE,{"blendedFrom":[makeQuery(id+"F7.boolean.opBoolean","COPY",EDGE,{"derivedFrom":makeQuery(id+"F7.opExtrude","CAP_EDGE",EDGE,{"disambiguationData":[OSD([sQuery(id+"F6.wireOp",EDGE,"E120.0.1.1")])],"isStart":false})}),makeQuery(id+"F4.opExtrude","CAP_FACE",FACE,{"disambiguationData":[OSD([sQuery(id+"F3.wireOp",EDGE,"E112.bottom"),sQuery(id+"F3.wireOp",EDGE,"E112.top"),sQuery(id+"F3.wireOp",EDGE,"E112.left"),sQuery(id+"F3.wireOp",EDGE,"E112.right"),sQuery(id+"F3.wireOp",EDGE,"E113.bottom"),sQuery(id+"F3.wireOp",EDGE,"E113.left"),sQuery(id+"F3.wireOp",EDGE,"E113.right"),sQuery(id+"F3.wireOp",EDGE,"E114.trimOffspring"),sQuery(id+"F3.wireOp",EDGE,"E115.filletArc"),sQuery(id+"F3.wireOp",EDGE,"E116.filletArc"),sQuery(id+"F3.wireOp",EDGE,"E117.filletArc"),sQuery(id+"F3.wireOp",EDGE,"E118.filletArc")])],"isStart":true})],"blendedInto":[makeQuery(id+"F4.opExtrude","CAP_FACE",FACE,{"disambiguationData":[OSD([sQuery(id+"F3.wireOp",EDGE,"E112.bottom"),sQuery(id+"F3.wireOp",EDGE,"E112.top"),sQuery(id+"F3.wireOp",EDGE,"E112.left"),sQuery(id+"F3.wireOp",EDGE,"E112.right"),sQuery(id+"F3.wireOp",EDGE,"E113.bottom"),sQuery(id+"F3.wireOp",EDGE,"E113.left"),sQuery(id+"F3.wireOp",EDGE,"E113.right"),sQuery(id+"F3.wireOp",EDGE,"E114.trimOffspring"),sQuery(id+"F3.wireOp",EDGE,"E115.filletArc"),sQuery(id+"F3.wireOp",EDGE,"E116.filletArc"),sQuery(id+"F3.wireOp",EDGE,"E117.filletArc"),sQuery(id+"F3.wireOp",EDGE,"E118.filletArc")])],"isStart":true})]});
            var Q1;
            Q1=makeQuery(id+"F8.opFillet","BLEND_EDGE",EDGE,{"blendedFrom":[makeQuery(id+"F7.boolean.opBoolean","COPY",EDGE,{"derivedFrom":makeQuery(id+"F7.opExtrude","CAP_EDGE",EDGE,{"disambiguationData":[OSD([sQuery(id+"F6.wireOp",EDGE,"E120.0.1.0")])],"isStart":false})}),makeQuery(id+"F4.opExtrude","CAP_FACE",FACE,{"disambiguationData":[OSD([sQuery(id+"F3.wireOp",EDGE,"E112.bottom"),sQuery(id+"F3.wireOp",EDGE,"E112.top"),sQuery(id+"F3.wireOp",EDGE,"E112.left"),sQuery(id+"F3.wireOp",EDGE,"E112.right"),sQuery(id+"F3.wireOp",EDGE,"E113.bottom"),sQuery(id+"F3.wireOp",EDGE,"E113.left"),sQuery(id+"F3.wireOp",EDGE,"E113.right"),sQuery(id+"F3.wireOp",EDGE,"E114.trimOffspring"),sQuery(id+"F3.wireOp",EDGE,"E115.filletArc"),sQuery(id+"F3.wireOp",EDGE,"E116.filletArc"),sQuery(id+"F3.wireOp",EDGE,"E117.filletArc"),sQuery(id+"F3.wireOp",EDGE,"E118.filletArc")])],"isStart":true})],"blendedInto":[makeQuery(id+"F4.opExtrude","CAP_FACE",FACE,{"disambiguationData":[OSD([sQuery(id+"F3.wireOp",EDGE,"E112.bottom"),sQuery(id+"F3.wireOp",EDGE,"E112.top"),sQuery(id+"F3.wireOp",EDGE,"E112.left"),sQuery(id+"F3.wireOp",EDGE,"E112.right"),sQuery(id+"F3.wireOp",EDGE,"E113.bottom"),sQuery(id+"F3.wireOp",EDGE,"E113.left"),sQuery(id+"F3.wireOp",EDGE,"E113.right"),sQuery(id+"F3.wireOp",EDGE,"E114.trimOffspring"),sQuery(id+"F3.wireOp",EDGE,"E115.filletArc"),sQuery(id+"F3.wireOp",EDGE,"E116.filletArc"),sQuery(id+"F3.wireOp",EDGE,"E117.filletArc"),sQuery(id+"F3.wireOp",EDGE,"E118.filletArc")])],"isStart":true})]});
            var Q2;
            Q2=makeQuery(id+"F8.opFillet","BLEND_EDGE",EDGE,{"blendedFrom":[makeQuery(id+"F7.boolean.opBoolean","COPY",EDGE,{"derivedFrom":makeQuery(id+"F7.opExtrude","CAP_EDGE",EDGE,{"disambiguationData":[OSD([sQuery(id+"F6.wireOp",EDGE,"E120.0.1.2")])],"isStart":false})}),makeQuery(id+"F4.opExtrude","CAP_FACE",FACE,{"disambiguationData":[OSD([sQuery(id+"F3.wireOp",EDGE,"E112.bottom"),sQuery(id+"F3.wireOp",EDGE,"E112.top"),sQuery(id+"F3.wireOp",EDGE,"E112.left"),sQuery(id+"F3.wireOp",EDGE,"E112.right"),sQuery(id+"F3.wireOp",EDGE,"E113.bottom"),sQuery(id+"F3.wireOp",EDGE,"E113.left"),sQuery(id+"F3.wireOp",EDGE,"E113.right"),sQuery(id+"F3.wireOp",EDGE,"E114.trimOffspring"),sQuery(id+"F3.wireOp",EDGE,"E115.filletArc"),sQuery(id+"F3.wireOp",EDGE,"E116.filletArc"),sQuery(id+"F3.wireOp",EDGE,"E117.filletArc"),sQuery(id+"F3.wireOp",EDGE,"E118.filletArc")])],"isStart":true})],"blendedInto":[makeQuery(id+"F4.opExtrude","CAP_FACE",FACE,{"disambiguationData":[OSD([sQuery(id+"F3.wireOp",EDGE,"E112.bottom"),sQuery(id+"F3.wireOp",EDGE,"E112.top"),sQuery(id+"F3.wireOp",EDGE,"E112.left"),sQuery(id+"F3.wireOp",EDGE,"E112.right"),sQuery(id+"F3.wireOp",EDGE,"E113.bottom"),sQuery(id+"F3.wireOp",EDGE,"E113.left"),sQuery(id+"F3.wireOp",EDGE,"E113.right"),sQuery(id+"F3.wireOp",EDGE,"E114.trimOffspring"),sQuery(id+"F3.wireOp",EDGE,"E115.filletArc"),sQuery(id+"F3.wireOp",EDGE,"E116.filletArc"),sQuery(id+"F3.wireOp",EDGE,"E117.filletArc"),sQuery(id+"F3.wireOp",EDGE,"E118.filletArc")])],"isStart":true})]});
            var Q3;
            Q3=makeQuery(id+"F8.opFillet","BLEND_EDGE",EDGE,{"blendedFrom":[makeQuery(id+"F7.boolean.opBoolean","COPY",EDGE,{"derivedFrom":makeQuery(id+"F7.opExtrude","CAP_EDGE",EDGE,{"disambiguationData":[OSD([sQuery(id+"F6.wireOp",EDGE,"E119.top")])],"isStart":false})}),makeQuery(id+"F4.opExtrude","CAP_FACE",FACE,{"disambiguationData":[OSD([sQuery(id+"F3.wireOp",EDGE,"E112.bottom"),sQuery(id+"F3.wireOp",EDGE,"E112.top"),sQuery(id+"F3.wireOp",EDGE,"E112.left"),sQuery(id+"F3.wireOp",EDGE,"E112.right"),sQuery(id+"F3.wireOp",EDGE,"E113.bottom"),sQuery(id+"F3.wireOp",EDGE,"E113.left"),sQuery(id+"F3.wireOp",EDGE,"E113.right"),sQuery(id+"F3.wireOp",EDGE,"E114.trimOffspring"),sQuery(id+"F3.wireOp",EDGE,"E115.filletArc"),sQuery(id+"F3.wireOp",EDGE,"E116.filletArc"),sQuery(id+"F3.wireOp",EDGE,"E117.filletArc"),sQuery(id+"F3.wireOp",EDGE,"E118.filletArc")])],"isStart":true})],"blendedInto":[makeQuery(id+"F4.opExtrude","CAP_FACE",FACE,{"disambiguationData":[OSD([sQuery(id+"F3.wireOp",EDGE,"E112.bottom"),sQuery(id+"F3.wireOp",EDGE,"E112.top"),sQuery(id+"F3.wireOp",EDGE,"E112.left"),sQuery(id+"F3.wireOp",EDGE,"E112.right"),sQuery(id+"F3.wireOp",EDGE,"E113.bottom"),sQuery(id+"F3.wireOp",EDGE,"E113.left"),sQuery(id+"F3.wireOp",EDGE,"E113.right"),sQuery(id+"F3.wireOp",EDGE,"E114.trimOffspring"),sQuery(id+"F3.wireOp",EDGE,"E115.filletArc"),sQuery(id+"F3.wireOp",EDGE,"E116.filletArc"),sQuery(id+"F3.wireOp",EDGE,"E117.filletArc"),sQuery(id+"F3.wireOp",EDGE,"E118.filletArc")])],"isStart":true})]});
            var Q4;
            Q4=makeQuery(id+"F8.opFillet","BLEND_EDGE",EDGE,{"blendedFrom":[makeQuery(id+"F7.boolean.opBoolean","COPY",EDGE,{"derivedFrom":makeQuery(id+"F7.opExtrude","CAP_EDGE",EDGE,{"disambiguationData":[OSD([sQuery(id+"F6.wireOp",EDGE,"E119.right")])],"isStart":false})}),makeQuery(id+"F4.opExtrude","CAP_FACE",FACE,{"disambiguationData":[OSD([sQuery(id+"F3.wireOp",EDGE,"E112.bottom"),sQuery(id+"F3.wireOp",EDGE,"E112.top"),sQuery(id+"F3.wireOp",EDGE,"E112.left"),sQuery(id+"F3.wireOp",EDGE,"E112.right"),sQuery(id+"F3.wireOp",EDGE,"E113.bottom"),sQuery(id+"F3.wireOp",EDGE,"E113.left"),sQuery(id+"F3.wireOp",EDGE,"E113.right"),sQuery(id+"F3.wireOp",EDGE,"E114.trimOffspring"),sQuery(id+"F3.wireOp",EDGE,"E115.filletArc"),sQuery(id+"F3.wireOp",EDGE,"E116.filletArc"),sQuery(id+"F3.wireOp",EDGE,"E117.filletArc"),sQuery(id+"F3.wireOp",EDGE,"E118.filletArc")])],"isStart":true})],"blendedInto":[makeQuery(id+"F4.opExtrude","CAP_FACE",FACE,{"disambiguationData":[OSD([sQuery(id+"F3.wireOp",EDGE,"E112.bottom"),sQuery(id+"F3.wireOp",EDGE,"E112.top"),sQuery(id+"F3.wireOp",EDGE,"E112.left"),sQuery(id+"F3.wireOp",EDGE,"E112.right"),sQuery(id+"F3.wireOp",EDGE,"E113.bottom"),sQuery(id+"F3.wireOp",EDGE,"E113.left"),sQuery(id+"F3.wireOp",EDGE,"E113.right"),sQuery(id+"F3.wireOp",EDGE,"E114.trimOffspring"),sQuery(id+"F3.wireOp",EDGE,"E115.filletArc"),sQuery(id+"F3.wireOp",EDGE,"E116.filletArc"),sQuery(id+"F3.wireOp",EDGE,"E117.filletArc"),sQuery(id+"F3.wireOp",EDGE,"E118.filletArc")])],"isStart":true})]});
            var Q5;
            Q5=makeQuery(id+"F8.opFillet","BLEND_EDGE",EDGE,{"blendedFrom":[makeQuery(id+"F7.boolean.opBoolean","COPY",EDGE,{"derivedFrom":makeQuery(id+"F7.opExtrude","CAP_EDGE",EDGE,{"disambiguationData":[OSD([sQuery(id+"F6.wireOp",EDGE,"E119.bottom")])],"isStart":false})}),makeQuery(id+"F4.opExtrude","CAP_FACE",FACE,{"disambiguationData":[OSD([sQuery(id+"F3.wireOp",EDGE,"E112.bottom"),sQuery(id+"F3.wireOp",EDGE,"E112.top"),sQuery(id+"F3.wireOp",EDGE,"E112.left"),sQuery(id+"F3.wireOp",EDGE,"E112.right"),sQuery(id+"F3.wireOp",EDGE,"E113.bottom"),sQuery(id+"F3.wireOp",EDGE,"E113.left"),sQuery(id+"F3.wireOp",EDGE,"E113.right"),sQuery(id+"F3.wireOp",EDGE,"E114.trimOffspring"),sQuery(id+"F3.wireOp",EDGE,"E115.filletArc"),sQuery(id+"F3.wireOp",EDGE,"E116.filletArc"),sQuery(id+"F3.wireOp",EDGE,"E117.filletArc"),sQuery(id+"F3.wireOp",EDGE,"E118.filletArc")])],"isStart":true})],"blendedInto":[makeQuery(id+"F4.opExtrude","CAP_FACE",FACE,{"disambiguationData":[OSD([sQuery(id+"F3.wireOp",EDGE,"E112.bottom"),sQuery(id+"F3.wireOp",EDGE,"E112.top"),sQuery(id+"F3.wireOp",EDGE,"E112.left"),sQuery(id+"F3.wireOp",EDGE,"E112.right"),sQuery(id+"F3.wireOp",EDGE,"E113.bottom"),sQuery(id+"F3.wireOp",EDGE,"E113.left"),sQuery(id+"F3.wireOp",EDGE,"E113.right"),sQuery(id+"F3.wireOp",EDGE,"E114.trimOffspring"),sQuery(id+"F3.wireOp",EDGE,"E115.filletArc"),sQuery(id+"F3.wireOp",EDGE,"E116.filletArc"),sQuery(id+"F3.wireOp",EDGE,"E117.filletArc"),sQuery(id+"F3.wireOp",EDGE,"E118.filletArc")])],"isStart":true})]});
            var Q6;
            Q6=makeQuery(id+"F8.opFillet","BLEND_EDGE",EDGE,{"blendedFrom":[makeQuery(id+"F7.boolean.opBoolean","COPY",EDGE,{"derivedFrom":makeQuery(id+"F7.opExtrude","CAP_EDGE",EDGE,{"disambiguationData":[OSD([sQuery(id+"F6.wireOp",EDGE,"E120.0.2.1")])],"isStart":false})}),makeQuery(id+"F4.opExtrude","CAP_FACE",FACE,{"disambiguationData":[OSD([sQuery(id+"F3.wireOp",EDGE,"E112.bottom"),sQuery(id+"F3.wireOp",EDGE,"E112.top"),sQuery(id+"F3.wireOp",EDGE,"E112.left"),sQuery(id+"F3.wireOp",EDGE,"E112.right"),sQuery(id+"F3.wireOp",EDGE,"E113.bottom"),sQuery(id+"F3.wireOp",EDGE,"E113.left"),sQuery(id+"F3.wireOp",EDGE,"E113.right"),sQuery(id+"F3.wireOp",EDGE,"E114.trimOffspring"),sQuery(id+"F3.wireOp",EDGE,"E115.filletArc"),sQuery(id+"F3.wireOp",EDGE,"E116.filletArc"),sQuery(id+"F3.wireOp",EDGE,"E117.filletArc"),sQuery(id+"F3.wireOp",EDGE,"E118.filletArc")])],"isStart":true})],"blendedInto":[makeQuery(id+"F4.opExtrude","CAP_FACE",FACE,{"disambiguationData":[OSD([sQuery(id+"F3.wireOp",EDGE,"E112.bottom"),sQuery(id+"F3.wireOp",EDGE,"E112.top"),sQuery(id+"F3.wireOp",EDGE,"E112.left"),sQuery(id+"F3.wireOp",EDGE,"E112.right"),sQuery(id+"F3.wireOp",EDGE,"E113.bottom"),sQuery(id+"F3.wireOp",EDGE,"E113.left"),sQuery(id+"F3.wireOp",EDGE,"E113.right"),sQuery(id+"F3.wireOp",EDGE,"E114.trimOffspring"),sQuery(id+"F3.wireOp",EDGE,"E115.filletArc"),sQuery(id+"F3.wireOp",EDGE,"E116.filletArc"),sQuery(id+"F3.wireOp",EDGE,"E117.filletArc"),sQuery(id+"F3.wireOp",EDGE,"E118.filletArc")])],"isStart":true})]});
            var Q7;
            Q7=makeQuery(id+"F8.opFillet","BLEND_EDGE",EDGE,{"blendedFrom":[makeQuery(id+"F7.boolean.opBoolean","COPY",EDGE,{"derivedFrom":makeQuery(id+"F7.opExtrude","CAP_EDGE",EDGE,{"disambiguationData":[OSD([sQuery(id+"F6.wireOp",EDGE,"E120.0.2.0")])],"isStart":false})}),makeQuery(id+"F4.opExtrude","CAP_FACE",FACE,{"disambiguationData":[OSD([sQuery(id+"F3.wireOp",EDGE,"E112.bottom"),sQuery(id+"F3.wireOp",EDGE,"E112.top"),sQuery(id+"F3.wireOp",EDGE,"E112.left"),sQuery(id+"F3.wireOp",EDGE,"E112.right"),sQuery(id+"F3.wireOp",EDGE,"E113.bottom"),sQuery(id+"F3.wireOp",EDGE,"E113.left"),sQuery(id+"F3.wireOp",EDGE,"E113.right"),sQuery(id+"F3.wireOp",EDGE,"E114.trimOffspring"),sQuery(id+"F3.wireOp",EDGE,"E115.filletArc"),sQuery(id+"F3.wireOp",EDGE,"E116.filletArc"),sQuery(id+"F3.wireOp",EDGE,"E117.filletArc"),sQuery(id+"F3.wireOp",EDGE,"E118.filletArc")])],"isStart":true})],"blendedInto":[makeQuery(id+"F4.opExtrude","CAP_FACE",FACE,{"disambiguationData":[OSD([sQuery(id+"F3.wireOp",EDGE,"E112.bottom"),sQuery(id+"F3.wireOp",EDGE,"E112.top"),sQuery(id+"F3.wireOp",EDGE,"E112.left"),sQuery(id+"F3.wireOp",EDGE,"E112.right"),sQuery(id+"F3.wireOp",EDGE,"E113.bottom"),sQuery(id+"F3.wireOp",EDGE,"E113.left"),sQuery(id+"F3.wireOp",EDGE,"E113.right"),sQuery(id+"F3.wireOp",EDGE,"E114.trimOffspring"),sQuery(id+"F3.wireOp",EDGE,"E115.filletArc"),sQuery(id+"F3.wireOp",EDGE,"E116.filletArc"),sQuery(id+"F3.wireOp",EDGE,"E117.filletArc"),sQuery(id+"F3.wireOp",EDGE,"E118.filletArc")])],"isStart":true})]});
            var Q8;
            Q8=makeQuery(id+"F8.opFillet","BLEND_EDGE",EDGE,{"blendedFrom":[makeQuery(id+"F7.boolean.opBoolean","COPY",EDGE,{"derivedFrom":makeQuery(id+"F7.opExtrude","CAP_EDGE",EDGE,{"disambiguationData":[OSD([sQuery(id+"F6.wireOp",EDGE,"E120.0.2.2")])],"isStart":false})}),makeQuery(id+"F4.opExtrude","CAP_FACE",FACE,{"disambiguationData":[OSD([sQuery(id+"F3.wireOp",EDGE,"E112.bottom"),sQuery(id+"F3.wireOp",EDGE,"E112.top"),sQuery(id+"F3.wireOp",EDGE,"E112.left"),sQuery(id+"F3.wireOp",EDGE,"E112.right"),sQuery(id+"F3.wireOp",EDGE,"E113.bottom"),sQuery(id+"F3.wireOp",EDGE,"E113.left"),sQuery(id+"F3.wireOp",EDGE,"E113.right"),sQuery(id+"F3.wireOp",EDGE,"E114.trimOffspring"),sQuery(id+"F3.wireOp",EDGE,"E115.filletArc"),sQuery(id+"F3.wireOp",EDGE,"E116.filletArc"),sQuery(id+"F3.wireOp",EDGE,"E117.filletArc"),sQuery(id+"F3.wireOp",EDGE,"E118.filletArc")])],"isStart":true})],"blendedInto":[makeQuery(id+"F4.opExtrude","CAP_FACE",FACE,{"disambiguationData":[OSD([sQuery(id+"F3.wireOp",EDGE,"E112.bottom"),sQuery(id+"F3.wireOp",EDGE,"E112.top"),sQuery(id+"F3.wireOp",EDGE,"E112.left"),sQuery(id+"F3.wireOp",EDGE,"E112.right"),sQuery(id+"F3.wireOp",EDGE,"E113.bottom"),sQuery(id+"F3.wireOp",EDGE,"E113.left"),sQuery(id+"F3.wireOp",EDGE,"E113.right"),sQuery(id+"F3.wireOp",EDGE,"E114.trimOffspring"),sQuery(id+"F3.wireOp",EDGE,"E115.filletArc"),sQuery(id+"F3.wireOp",EDGE,"E116.filletArc"),sQuery(id+"F3.wireOp",EDGE,"E117.filletArc"),sQuery(id+"F3.wireOp",EDGE,"E118.filletArc")])],"isStart":true})]});
            var Q9;
            Q9=makeQuery(id+"F8.opFillet","BLEND_EDGE",EDGE,{"blendedFrom":[makeQuery(id+"F7.boolean.opBoolean","COPY",EDGE,{"derivedFrom":makeQuery(id+"F7.opExtrude","CAP_EDGE",EDGE,{"disambiguationData":[OSD([sQuery(id+"F6.wireOp",EDGE,"E120.0.3.1")])],"isStart":false})}),makeQuery(id+"F4.opExtrude","CAP_FACE",FACE,{"disambiguationData":[OSD([sQuery(id+"F3.wireOp",EDGE,"E112.bottom"),sQuery(id+"F3.wireOp",EDGE,"E112.top"),sQuery(id+"F3.wireOp",EDGE,"E112.left"),sQuery(id+"F3.wireOp",EDGE,"E112.right"),sQuery(id+"F3.wireOp",EDGE,"E113.bottom"),sQuery(id+"F3.wireOp",EDGE,"E113.left"),sQuery(id+"F3.wireOp",EDGE,"E113.right"),sQuery(id+"F3.wireOp",EDGE,"E114.trimOffspring"),sQuery(id+"F3.wireOp",EDGE,"E115.filletArc"),sQuery(id+"F3.wireOp",EDGE,"E116.filletArc"),sQuery(id+"F3.wireOp",EDGE,"E117.filletArc"),sQuery(id+"F3.wireOp",EDGE,"E118.filletArc")])],"isStart":true})],"blendedInto":[makeQuery(id+"F4.opExtrude","CAP_FACE",FACE,{"disambiguationData":[OSD([sQuery(id+"F3.wireOp",EDGE,"E112.bottom"),sQuery(id+"F3.wireOp",EDGE,"E112.top"),sQuery(id+"F3.wireOp",EDGE,"E112.left"),sQuery(id+"F3.wireOp",EDGE,"E112.right"),sQuery(id+"F3.wireOp",EDGE,"E113.bottom"),sQuery(id+"F3.wireOp",EDGE,"E113.left"),sQuery(id+"F3.wireOp",EDGE,"E113.right"),sQuery(id+"F3.wireOp",EDGE,"E114.trimOffspring"),sQuery(id+"F3.wireOp",EDGE,"E115.filletArc"),sQuery(id+"F3.wireOp",EDGE,"E116.filletArc"),sQuery(id+"F3.wireOp",EDGE,"E117.filletArc"),sQuery(id+"F3.wireOp",EDGE,"E118.filletArc")])],"isStart":true})]});
            var Q10;
            Q10=makeQuery(id+"F8.opFillet","BLEND_EDGE",EDGE,{"blendedFrom":[makeQuery(id+"F7.boolean.opBoolean","COPY",EDGE,{"derivedFrom":makeQuery(id+"F7.opExtrude","CAP_EDGE",EDGE,{"disambiguationData":[OSD([sQuery(id+"F6.wireOp",EDGE,"E120.0.3.2")])],"isStart":false})}),makeQuery(id+"F4.opExtrude","CAP_FACE",FACE,{"disambiguationData":[OSD([sQuery(id+"F3.wireOp",EDGE,"E112.bottom"),sQuery(id+"F3.wireOp",EDGE,"E112.top"),sQuery(id+"F3.wireOp",EDGE,"E112.left"),sQuery(id+"F3.wireOp",EDGE,"E112.right"),sQuery(id+"F3.wireOp",EDGE,"E113.bottom"),sQuery(id+"F3.wireOp",EDGE,"E113.left"),sQuery(id+"F3.wireOp",EDGE,"E113.right"),sQuery(id+"F3.wireOp",EDGE,"E114.trimOffspring"),sQuery(id+"F3.wireOp",EDGE,"E115.filletArc"),sQuery(id+"F3.wireOp",EDGE,"E116.filletArc"),sQuery(id+"F3.wireOp",EDGE,"E117.filletArc"),sQuery(id+"F3.wireOp",EDGE,"E118.filletArc")])],"isStart":true})],"blendedInto":[makeQuery(id+"F4.opExtrude","CAP_FACE",FACE,{"disambiguationData":[OSD([sQuery(id+"F3.wireOp",EDGE,"E112.bottom"),sQuery(id+"F3.wireOp",EDGE,"E112.top"),sQuery(id+"F3.wireOp",EDGE,"E112.left"),sQuery(id+"F3.wireOp",EDGE,"E112.right"),sQuery(id+"F3.wireOp",EDGE,"E113.bottom"),sQuery(id+"F3.wireOp",EDGE,"E113.left"),sQuery(id+"F3.wireOp",EDGE,"E113.right"),sQuery(id+"F3.wireOp",EDGE,"E114.trimOffspring"),sQuery(id+"F3.wireOp",EDGE,"E115.filletArc"),sQuery(id+"F3.wireOp",EDGE,"E116.filletArc"),sQuery(id+"F3.wireOp",EDGE,"E117.filletArc"),sQuery(id+"F3.wireOp",EDGE,"E118.filletArc")])],"isStart":true})]});
            var Q11;
            Q11=makeQuery(id+"F8.opFillet","BLEND_EDGE",EDGE,{"blendedFrom":[makeQuery(id+"F7.boolean.opBoolean","COPY",EDGE,{"derivedFrom":makeQuery(id+"F7.opExtrude","CAP_EDGE",EDGE,{"disambiguationData":[OSD([sQuery(id+"F6.wireOp",EDGE,"E120.0.3.0")])],"isStart":false})}),makeQuery(id+"F4.opExtrude","CAP_FACE",FACE,{"disambiguationData":[OSD([sQuery(id+"F3.wireOp",EDGE,"E112.bottom"),sQuery(id+"F3.wireOp",EDGE,"E112.top"),sQuery(id+"F3.wireOp",EDGE,"E112.left"),sQuery(id+"F3.wireOp",EDGE,"E112.right"),sQuery(id+"F3.wireOp",EDGE,"E113.bottom"),sQuery(id+"F3.wireOp",EDGE,"E113.left"),sQuery(id+"F3.wireOp",EDGE,"E113.right"),sQuery(id+"F3.wireOp",EDGE,"E114.trimOffspring"),sQuery(id+"F3.wireOp",EDGE,"E115.filletArc"),sQuery(id+"F3.wireOp",EDGE,"E116.filletArc"),sQuery(id+"F3.wireOp",EDGE,"E117.filletArc"),sQuery(id+"F3.wireOp",EDGE,"E118.filletArc")])],"isStart":true})],"blendedInto":[makeQuery(id+"F4.opExtrude","CAP_FACE",FACE,{"disambiguationData":[OSD([sQuery(id+"F3.wireOp",EDGE,"E112.bottom"),sQuery(id+"F3.wireOp",EDGE,"E112.top"),sQuery(id+"F3.wireOp",EDGE,"E112.left"),sQuery(id+"F3.wireOp",EDGE,"E112.right"),sQuery(id+"F3.wireOp",EDGE,"E113.bottom"),sQuery(id+"F3.wireOp",EDGE,"E113.left"),sQuery(id+"F3.wireOp",EDGE,"E113.right"),sQuery(id+"F3.wireOp",EDGE,"E114.trimOffspring"),sQuery(id+"F3.wireOp",EDGE,"E115.filletArc"),sQuery(id+"F3.wireOp",EDGE,"E116.filletArc"),sQuery(id+"F3.wireOp",EDGE,"E117.filletArc"),sQuery(id+"F3.wireOp",EDGE,"E118.filletArc")])],"isStart":true})]});
            var Q12;
            Q12=makeQuery(id+"F8.opFillet","BLEND_EDGE",EDGE,{"blendedFrom":[makeQuery(id+"F7.boolean.opBoolean","COPY",EDGE,{"derivedFrom":makeQuery(id+"F7.opExtrude","CAP_EDGE",EDGE,{"disambiguationData":[OSD([sQuery(id+"F6.wireOp",EDGE,"E120.0.4.2")])],"isStart":false})}),makeQuery(id+"F4.opExtrude","CAP_FACE",FACE,{"disambiguationData":[OSD([sQuery(id+"F3.wireOp",EDGE,"E112.bottom"),sQuery(id+"F3.wireOp",EDGE,"E112.top"),sQuery(id+"F3.wireOp",EDGE,"E112.left"),sQuery(id+"F3.wireOp",EDGE,"E112.right"),sQuery(id+"F3.wireOp",EDGE,"E113.bottom"),sQuery(id+"F3.wireOp",EDGE,"E113.left"),sQuery(id+"F3.wireOp",EDGE,"E113.right"),sQuery(id+"F3.wireOp",EDGE,"E114.trimOffspring"),sQuery(id+"F3.wireOp",EDGE,"E115.filletArc"),sQuery(id+"F3.wireOp",EDGE,"E116.filletArc"),sQuery(id+"F3.wireOp",EDGE,"E117.filletArc"),sQuery(id+"F3.wireOp",EDGE,"E118.filletArc")])],"isStart":true})],"blendedInto":[makeQuery(id+"F4.opExtrude","CAP_FACE",FACE,{"disambiguationData":[OSD([sQuery(id+"F3.wireOp",EDGE,"E112.bottom"),sQuery(id+"F3.wireOp",EDGE,"E112.top"),sQuery(id+"F3.wireOp",EDGE,"E112.left"),sQuery(id+"F3.wireOp",EDGE,"E112.right"),sQuery(id+"F3.wireOp",EDGE,"E113.bottom"),sQuery(id+"F3.wireOp",EDGE,"E113.left"),sQuery(id+"F3.wireOp",EDGE,"E113.right"),sQuery(id+"F3.wireOp",EDGE,"E114.trimOffspring"),sQuery(id+"F3.wireOp",EDGE,"E115.filletArc"),sQuery(id+"F3.wireOp",EDGE,"E116.filletArc"),sQuery(id+"F3.wireOp",EDGE,"E117.filletArc"),sQuery(id+"F3.wireOp",EDGE,"E118.filletArc")])],"isStart":true})]});
            var Q13;
            Q13=makeQuery(id+"F8.opFillet","BLEND_EDGE",EDGE,{"blendedFrom":[makeQuery(id+"F7.boolean.opBoolean","COPY",EDGE,{"derivedFrom":makeQuery(id+"F7.opExtrude","CAP_EDGE",EDGE,{"disambiguationData":[OSD([sQuery(id+"F6.wireOp",EDGE,"E120.0.5.2")])],"isStart":false})}),makeQuery(id+"F4.opExtrude","CAP_FACE",FACE,{"disambiguationData":[OSD([sQuery(id+"F3.wireOp",EDGE,"E112.bottom"),sQuery(id+"F3.wireOp",EDGE,"E112.top"),sQuery(id+"F3.wireOp",EDGE,"E112.left"),sQuery(id+"F3.wireOp",EDGE,"E112.right"),sQuery(id+"F3.wireOp",EDGE,"E113.bottom"),sQuery(id+"F3.wireOp",EDGE,"E113.left"),sQuery(id+"F3.wireOp",EDGE,"E113.right"),sQuery(id+"F3.wireOp",EDGE,"E114.trimOffspring"),sQuery(id+"F3.wireOp",EDGE,"E115.filletArc"),sQuery(id+"F3.wireOp",EDGE,"E116.filletArc"),sQuery(id+"F3.wireOp",EDGE,"E117.filletArc"),sQuery(id+"F3.wireOp",EDGE,"E118.filletArc")])],"isStart":true})],"blendedInto":[makeQuery(id+"F4.opExtrude","CAP_FACE",FACE,{"disambiguationData":[OSD([sQuery(id+"F3.wireOp",EDGE,"E112.bottom"),sQuery(id+"F3.wireOp",EDGE,"E112.top"),sQuery(id+"F3.wireOp",EDGE,"E112.left"),sQuery(id+"F3.wireOp",EDGE,"E112.right"),sQuery(id+"F3.wireOp",EDGE,"E113.bottom"),sQuery(id+"F3.wireOp",EDGE,"E113.left"),sQuery(id+"F3.wireOp",EDGE,"E113.right"),sQuery(id+"F3.wireOp",EDGE,"E114.trimOffspring"),sQuery(id+"F3.wireOp",EDGE,"E115.filletArc"),sQuery(id+"F3.wireOp",EDGE,"E116.filletArc"),sQuery(id+"F3.wireOp",EDGE,"E117.filletArc"),sQuery(id+"F3.wireOp",EDGE,"E118.filletArc")])],"isStart":true})]});
            var Q14;
            Q14=makeQuery(id+"F8.opFillet","BLEND_EDGE",EDGE,{"blendedFrom":[makeQuery(id+"F7.boolean.opBoolean","COPY",EDGE,{"derivedFrom":makeQuery(id+"F7.opExtrude","CAP_EDGE",EDGE,{"disambiguationData":[OSD([sQuery(id+"F6.wireOp",EDGE,"E120.0.6.2")])],"isStart":false})}),makeQuery(id+"F4.opExtrude","CAP_FACE",FACE,{"disambiguationData":[OSD([sQuery(id+"F3.wireOp",EDGE,"E112.bottom"),sQuery(id+"F3.wireOp",EDGE,"E112.top"),sQuery(id+"F3.wireOp",EDGE,"E112.left"),sQuery(id+"F3.wireOp",EDGE,"E112.right"),sQuery(id+"F3.wireOp",EDGE,"E113.bottom"),sQuery(id+"F3.wireOp",EDGE,"E113.left"),sQuery(id+"F3.wireOp",EDGE,"E113.right"),sQuery(id+"F3.wireOp",EDGE,"E114.trimOffspring"),sQuery(id+"F3.wireOp",EDGE,"E115.filletArc"),sQuery(id+"F3.wireOp",EDGE,"E116.filletArc"),sQuery(id+"F3.wireOp",EDGE,"E117.filletArc"),sQuery(id+"F3.wireOp",EDGE,"E118.filletArc")])],"isStart":true})],"blendedInto":[makeQuery(id+"F4.opExtrude","CAP_FACE",FACE,{"disambiguationData":[OSD([sQuery(id+"F3.wireOp",EDGE,"E112.bottom"),sQuery(id+"F3.wireOp",EDGE,"E112.top"),sQuery(id+"F3.wireOp",EDGE,"E112.left"),sQuery(id+"F3.wireOp",EDGE,"E112.right"),sQuery(id+"F3.wireOp",EDGE,"E113.bottom"),sQuery(id+"F3.wireOp",EDGE,"E113.left"),sQuery(id+"F3.wireOp",EDGE,"E113.right"),sQuery(id+"F3.wireOp",EDGE,"E114.trimOffspring"),sQuery(id+"F3.wireOp",EDGE,"E115.filletArc"),sQuery(id+"F3.wireOp",EDGE,"E116.filletArc"),sQuery(id+"F3.wireOp",EDGE,"E117.filletArc"),sQuery(id+"F3.wireOp",EDGE,"E118.filletArc")])],"isStart":true})]});
            var Q15;
            Q15=makeQuery(id+"F8.opFillet","BLEND_EDGE",EDGE,{"blendedFrom":[makeQuery(id+"F7.boolean.opBoolean","COPY",EDGE,{"derivedFrom":makeQuery(id+"F7.opExtrude","CAP_EDGE",EDGE,{"disambiguationData":[OSD([sQuery(id+"F6.wireOp",EDGE,"E120.0.6.0")])],"isStart":false})}),makeQuery(id+"F4.opExtrude","CAP_FACE",FACE,{"disambiguationData":[OSD([sQuery(id+"F3.wireOp",EDGE,"E112.bottom"),sQuery(id+"F3.wireOp",EDGE,"E112.top"),sQuery(id+"F3.wireOp",EDGE,"E112.left"),sQuery(id+"F3.wireOp",EDGE,"E112.right"),sQuery(id+"F3.wireOp",EDGE,"E113.bottom"),sQuery(id+"F3.wireOp",EDGE,"E113.left"),sQuery(id+"F3.wireOp",EDGE,"E113.right"),sQuery(id+"F3.wireOp",EDGE,"E114.trimOffspring"),sQuery(id+"F3.wireOp",EDGE,"E115.filletArc"),sQuery(id+"F3.wireOp",EDGE,"E116.filletArc"),sQuery(id+"F3.wireOp",EDGE,"E117.filletArc"),sQuery(id+"F3.wireOp",EDGE,"E118.filletArc")])],"isStart":true})],"blendedInto":[makeQuery(id+"F4.opExtrude","CAP_FACE",FACE,{"disambiguationData":[OSD([sQuery(id+"F3.wireOp",EDGE,"E112.bottom"),sQuery(id+"F3.wireOp",EDGE,"E112.top"),sQuery(id+"F3.wireOp",EDGE,"E112.left"),sQuery(id+"F3.wireOp",EDGE,"E112.right"),sQuery(id+"F3.wireOp",EDGE,"E113.bottom"),sQuery(id+"F3.wireOp",EDGE,"E113.left"),sQuery(id+"F3.wireOp",EDGE,"E113.right"),sQuery(id+"F3.wireOp",EDGE,"E114.trimOffspring"),sQuery(id+"F3.wireOp",EDGE,"E115.filletArc"),sQuery(id+"F3.wireOp",EDGE,"E116.filletArc"),sQuery(id+"F3.wireOp",EDGE,"E117.filletArc"),sQuery(id+"F3.wireOp",EDGE,"E118.filletArc")])],"isStart":true})]});
            var Q16;
            Q16=makeQuery(id+"F8.opFillet","BLEND_EDGE",EDGE,{"blendedFrom":[makeQuery(id+"F7.boolean.opBoolean","COPY",EDGE,{"derivedFrom":makeQuery(id+"F7.opExtrude","CAP_EDGE",EDGE,{"disambiguationData":[OSD([sQuery(id+"F6.wireOp",EDGE,"E120.0.6.1")])],"isStart":false})}),makeQuery(id+"F4.opExtrude","CAP_FACE",FACE,{"disambiguationData":[OSD([sQuery(id+"F3.wireOp",EDGE,"E112.bottom"),sQuery(id+"F3.wireOp",EDGE,"E112.top"),sQuery(id+"F3.wireOp",EDGE,"E112.left"),sQuery(id+"F3.wireOp",EDGE,"E112.right"),sQuery(id+"F3.wireOp",EDGE,"E113.bottom"),sQuery(id+"F3.wireOp",EDGE,"E113.left"),sQuery(id+"F3.wireOp",EDGE,"E113.right"),sQuery(id+"F3.wireOp",EDGE,"E114.trimOffspring"),sQuery(id+"F3.wireOp",EDGE,"E115.filletArc"),sQuery(id+"F3.wireOp",EDGE,"E116.filletArc"),sQuery(id+"F3.wireOp",EDGE,"E117.filletArc"),sQuery(id+"F3.wireOp",EDGE,"E118.filletArc")])],"isStart":true})],"blendedInto":[makeQuery(id+"F4.opExtrude","CAP_FACE",FACE,{"disambiguationData":[OSD([sQuery(id+"F3.wireOp",EDGE,"E112.bottom"),sQuery(id+"F3.wireOp",EDGE,"E112.top"),sQuery(id+"F3.wireOp",EDGE,"E112.left"),sQuery(id+"F3.wireOp",EDGE,"E112.right"),sQuery(id+"F3.wireOp",EDGE,"E113.bottom"),sQuery(id+"F3.wireOp",EDGE,"E113.left"),sQuery(id+"F3.wireOp",EDGE,"E113.right"),sQuery(id+"F3.wireOp",EDGE,"E114.trimOffspring"),sQuery(id+"F3.wireOp",EDGE,"E115.filletArc"),sQuery(id+"F3.wireOp",EDGE,"E116.filletArc"),sQuery(id+"F3.wireOp",EDGE,"E117.filletArc"),sQuery(id+"F3.wireOp",EDGE,"E118.filletArc")])],"isStart":true})]});
            var Q17;
            Q17=makeQuery(id+"F8.opFillet","BLEND_EDGE",EDGE,{"blendedFrom":[makeQuery(id+"F7.boolean.opBoolean","COPY",EDGE,{"derivedFrom":makeQuery(id+"F7.opExtrude","CAP_EDGE",EDGE,{"disambiguationData":[OSD([sQuery(id+"F6.wireOp",EDGE,"E120.0.5.0")])],"isStart":false})}),makeQuery(id+"F4.opExtrude","CAP_FACE",FACE,{"disambiguationData":[OSD([sQuery(id+"F3.wireOp",EDGE,"E112.bottom"),sQuery(id+"F3.wireOp",EDGE,"E112.top"),sQuery(id+"F3.wireOp",EDGE,"E112.left"),sQuery(id+"F3.wireOp",EDGE,"E112.right"),sQuery(id+"F3.wireOp",EDGE,"E113.bottom"),sQuery(id+"F3.wireOp",EDGE,"E113.left"),sQuery(id+"F3.wireOp",EDGE,"E113.right"),sQuery(id+"F3.wireOp",EDGE,"E114.trimOffspring"),sQuery(id+"F3.wireOp",EDGE,"E115.filletArc"),sQuery(id+"F3.wireOp",EDGE,"E116.filletArc"),sQuery(id+"F3.wireOp",EDGE,"E117.filletArc"),sQuery(id+"F3.wireOp",EDGE,"E118.filletArc")])],"isStart":true})],"blendedInto":[makeQuery(id+"F4.opExtrude","CAP_FACE",FACE,{"disambiguationData":[OSD([sQuery(id+"F3.wireOp",EDGE,"E112.bottom"),sQuery(id+"F3.wireOp",EDGE,"E112.top"),sQuery(id+"F3.wireOp",EDGE,"E112.left"),sQuery(id+"F3.wireOp",EDGE,"E112.right"),sQuery(id+"F3.wireOp",EDGE,"E113.bottom"),sQuery(id+"F3.wireOp",EDGE,"E113.left"),sQuery(id+"F3.wireOp",EDGE,"E113.right"),sQuery(id+"F3.wireOp",EDGE,"E114.trimOffspring"),sQuery(id+"F3.wireOp",EDGE,"E115.filletArc"),sQuery(id+"F3.wireOp",EDGE,"E116.filletArc"),sQuery(id+"F3.wireOp",EDGE,"E117.filletArc"),sQuery(id+"F3.wireOp",EDGE,"E118.filletArc")])],"isStart":true})]});
            var Q18;
            Q18=makeQuery(id+"F8.opFillet","BLEND_EDGE",EDGE,{"blendedFrom":[makeQuery(id+"F7.boolean.opBoolean","COPY",EDGE,{"derivedFrom":makeQuery(id+"F7.opExtrude","CAP_EDGE",EDGE,{"disambiguationData":[OSD([sQuery(id+"F6.wireOp",EDGE,"E120.0.5.1")])],"isStart":false})}),makeQuery(id+"F4.opExtrude","CAP_FACE",FACE,{"disambiguationData":[OSD([sQuery(id+"F3.wireOp",EDGE,"E112.bottom"),sQuery(id+"F3.wireOp",EDGE,"E112.top"),sQuery(id+"F3.wireOp",EDGE,"E112.left"),sQuery(id+"F3.wireOp",EDGE,"E112.right"),sQuery(id+"F3.wireOp",EDGE,"E113.bottom"),sQuery(id+"F3.wireOp",EDGE,"E113.left"),sQuery(id+"F3.wireOp",EDGE,"E113.right"),sQuery(id+"F3.wireOp",EDGE,"E114.trimOffspring"),sQuery(id+"F3.wireOp",EDGE,"E115.filletArc"),sQuery(id+"F3.wireOp",EDGE,"E116.filletArc"),sQuery(id+"F3.wireOp",EDGE,"E117.filletArc"),sQuery(id+"F3.wireOp",EDGE,"E118.filletArc")])],"isStart":true})],"blendedInto":[makeQuery(id+"F4.opExtrude","CAP_FACE",FACE,{"disambiguationData":[OSD([sQuery(id+"F3.wireOp",EDGE,"E112.bottom"),sQuery(id+"F3.wireOp",EDGE,"E112.top"),sQuery(id+"F3.wireOp",EDGE,"E112.left"),sQuery(id+"F3.wireOp",EDGE,"E112.right"),sQuery(id+"F3.wireOp",EDGE,"E113.bottom"),sQuery(id+"F3.wireOp",EDGE,"E113.left"),sQuery(id+"F3.wireOp",EDGE,"E113.right"),sQuery(id+"F3.wireOp",EDGE,"E114.trimOffspring"),sQuery(id+"F3.wireOp",EDGE,"E115.filletArc"),sQuery(id+"F3.wireOp",EDGE,"E116.filletArc"),sQuery(id+"F3.wireOp",EDGE,"E117.filletArc"),sQuery(id+"F3.wireOp",EDGE,"E118.filletArc")])],"isStart":true})]});
            var Q19;
            Q19=makeQuery(id+"F8.opFillet","BLEND_EDGE",EDGE,{"blendedFrom":[makeQuery(id+"F7.boolean.opBoolean","COPY",EDGE,{"derivedFrom":makeQuery(id+"F7.opExtrude","CAP_EDGE",EDGE,{"disambiguationData":[OSD([sQuery(id+"F6.wireOp",EDGE,"E120.0.4.0")])],"isStart":false})}),makeQuery(id+"F4.opExtrude","CAP_FACE",FACE,{"disambiguationData":[OSD([sQuery(id+"F3.wireOp",EDGE,"E112.bottom"),sQuery(id+"F3.wireOp",EDGE,"E112.top"),sQuery(id+"F3.wireOp",EDGE,"E112.left"),sQuery(id+"F3.wireOp",EDGE,"E112.right"),sQuery(id+"F3.wireOp",EDGE,"E113.bottom"),sQuery(id+"F3.wireOp",EDGE,"E113.left"),sQuery(id+"F3.wireOp",EDGE,"E113.right"),sQuery(id+"F3.wireOp",EDGE,"E114.trimOffspring"),sQuery(id+"F3.wireOp",EDGE,"E115.filletArc"),sQuery(id+"F3.wireOp",EDGE,"E116.filletArc"),sQuery(id+"F3.wireOp",EDGE,"E117.filletArc"),sQuery(id+"F3.wireOp",EDGE,"E118.filletArc")])],"isStart":true})],"blendedInto":[makeQuery(id+"F4.opExtrude","CAP_FACE",FACE,{"disambiguationData":[OSD([sQuery(id+"F3.wireOp",EDGE,"E112.bottom"),sQuery(id+"F3.wireOp",EDGE,"E112.top"),sQuery(id+"F3.wireOp",EDGE,"E112.left"),sQuery(id+"F3.wireOp",EDGE,"E112.right"),sQuery(id+"F3.wireOp",EDGE,"E113.bottom"),sQuery(id+"F3.wireOp",EDGE,"E113.left"),sQuery(id+"F3.wireOp",EDGE,"E113.right"),sQuery(id+"F3.wireOp",EDGE,"E114.trimOffspring"),sQuery(id+"F3.wireOp",EDGE,"E115.filletArc"),sQuery(id+"F3.wireOp",EDGE,"E116.filletArc"),sQuery(id+"F3.wireOp",EDGE,"E117.filletArc"),sQuery(id+"F3.wireOp",EDGE,"E118.filletArc")])],"isStart":true})]});
            var Q20;
            Q20=makeQuery(id+"F8.opFillet","BLEND_EDGE",EDGE,{"blendedFrom":[makeQuery(id+"F7.boolean.opBoolean","COPY",EDGE,{"derivedFrom":makeQuery(id+"F7.opExtrude","CAP_EDGE",EDGE,{"disambiguationData":[OSD([sQuery(id+"F6.wireOp",EDGE,"E120.0.4.1")])],"isStart":false})}),makeQuery(id+"F4.opExtrude","CAP_FACE",FACE,{"disambiguationData":[OSD([sQuery(id+"F3.wireOp",EDGE,"E112.bottom"),sQuery(id+"F3.wireOp",EDGE,"E112.top"),sQuery(id+"F3.wireOp",EDGE,"E112.left"),sQuery(id+"F3.wireOp",EDGE,"E112.right"),sQuery(id+"F3.wireOp",EDGE,"E113.bottom"),sQuery(id+"F3.wireOp",EDGE,"E113.left"),sQuery(id+"F3.wireOp",EDGE,"E113.right"),sQuery(id+"F3.wireOp",EDGE,"E114.trimOffspring"),sQuery(id+"F3.wireOp",EDGE,"E115.filletArc"),sQuery(id+"F3.wireOp",EDGE,"E116.filletArc"),sQuery(id+"F3.wireOp",EDGE,"E117.filletArc"),sQuery(id+"F3.wireOp",EDGE,"E118.filletArc")])],"isStart":true})],"blendedInto":[makeQuery(id+"F4.opExtrude","CAP_FACE",FACE,{"disambiguationData":[OSD([sQuery(id+"F3.wireOp",EDGE,"E112.bottom"),sQuery(id+"F3.wireOp",EDGE,"E112.top"),sQuery(id+"F3.wireOp",EDGE,"E112.left"),sQuery(id+"F3.wireOp",EDGE,"E112.right"),sQuery(id+"F3.wireOp",EDGE,"E113.bottom"),sQuery(id+"F3.wireOp",EDGE,"E113.left"),sQuery(id+"F3.wireOp",EDGE,"E113.right"),sQuery(id+"F3.wireOp",EDGE,"E114.trimOffspring"),sQuery(id+"F3.wireOp",EDGE,"E115.filletArc"),sQuery(id+"F3.wireOp",EDGE,"E116.filletArc"),sQuery(id+"F3.wireOp",EDGE,"E117.filletArc"),sQuery(id+"F3.wireOp",EDGE,"E118.filletArc")])],"isStart":true})]});
            var Q21;
            Q21=makeQuery(id+"F8.opFillet","BLEND_EDGE",EDGE,{"blendedFrom":[makeQuery(id+"F7.boolean.opBoolean","COPY",EDGE,{"derivedFrom":makeQuery(id+"F7.opExtrude","CAP_EDGE",EDGE,{"disambiguationData":[OSD([sQuery(id+"F6.wireOp",EDGE,"E120.0.7.2")])],"isStart":false})}),makeQuery(id+"F4.opExtrude","CAP_FACE",FACE,{"disambiguationData":[OSD([sQuery(id+"F3.wireOp",EDGE,"E112.bottom"),sQuery(id+"F3.wireOp",EDGE,"E112.top"),sQuery(id+"F3.wireOp",EDGE,"E112.left"),sQuery(id+"F3.wireOp",EDGE,"E112.right"),sQuery(id+"F3.wireOp",EDGE,"E113.bottom"),sQuery(id+"F3.wireOp",EDGE,"E113.left"),sQuery(id+"F3.wireOp",EDGE,"E113.right"),sQuery(id+"F3.wireOp",EDGE,"E114.trimOffspring"),sQuery(id+"F3.wireOp",EDGE,"E115.filletArc"),sQuery(id+"F3.wireOp",EDGE,"E116.filletArc"),sQuery(id+"F3.wireOp",EDGE,"E117.filletArc"),sQuery(id+"F3.wireOp",EDGE,"E118.filletArc")])],"isStart":true})],"blendedInto":[makeQuery(id+"F4.opExtrude","CAP_FACE",FACE,{"disambiguationData":[OSD([sQuery(id+"F3.wireOp",EDGE,"E112.bottom"),sQuery(id+"F3.wireOp",EDGE,"E112.top"),sQuery(id+"F3.wireOp",EDGE,"E112.left"),sQuery(id+"F3.wireOp",EDGE,"E112.right"),sQuery(id+"F3.wireOp",EDGE,"E113.bottom"),sQuery(id+"F3.wireOp",EDGE,"E113.left"),sQuery(id+"F3.wireOp",EDGE,"E113.right"),sQuery(id+"F3.wireOp",EDGE,"E114.trimOffspring"),sQuery(id+"F3.wireOp",EDGE,"E115.filletArc"),sQuery(id+"F3.wireOp",EDGE,"E116.filletArc"),sQuery(id+"F3.wireOp",EDGE,"E117.filletArc"),sQuery(id+"F3.wireOp",EDGE,"E118.filletArc")])],"isStart":true})]});
            var Q22;
            Q22=makeQuery(id+"F8.opFillet","BLEND_EDGE",EDGE,{"blendedFrom":[makeQuery(id+"F7.boolean.opBoolean","COPY",EDGE,{"derivedFrom":makeQuery(id+"F7.opExtrude","CAP_EDGE",EDGE,{"disambiguationData":[OSD([sQuery(id+"F6.wireOp",EDGE,"E120.0.7.0")])],"isStart":false})}),makeQuery(id+"F4.opExtrude","CAP_FACE",FACE,{"disambiguationData":[OSD([sQuery(id+"F3.wireOp",EDGE,"E112.bottom"),sQuery(id+"F3.wireOp",EDGE,"E112.top"),sQuery(id+"F3.wireOp",EDGE,"E112.left"),sQuery(id+"F3.wireOp",EDGE,"E112.right"),sQuery(id+"F3.wireOp",EDGE,"E113.bottom"),sQuery(id+"F3.wireOp",EDGE,"E113.left"),sQuery(id+"F3.wireOp",EDGE,"E113.right"),sQuery(id+"F3.wireOp",EDGE,"E114.trimOffspring"),sQuery(id+"F3.wireOp",EDGE,"E115.filletArc"),sQuery(id+"F3.wireOp",EDGE,"E116.filletArc"),sQuery(id+"F3.wireOp",EDGE,"E117.filletArc"),sQuery(id+"F3.wireOp",EDGE,"E118.filletArc")])],"isStart":true})],"blendedInto":[makeQuery(id+"F4.opExtrude","CAP_FACE",FACE,{"disambiguationData":[OSD([sQuery(id+"F3.wireOp",EDGE,"E112.bottom"),sQuery(id+"F3.wireOp",EDGE,"E112.top"),sQuery(id+"F3.wireOp",EDGE,"E112.left"),sQuery(id+"F3.wireOp",EDGE,"E112.right"),sQuery(id+"F3.wireOp",EDGE,"E113.bottom"),sQuery(id+"F3.wireOp",EDGE,"E113.left"),sQuery(id+"F3.wireOp",EDGE,"E113.right"),sQuery(id+"F3.wireOp",EDGE,"E114.trimOffspring"),sQuery(id+"F3.wireOp",EDGE,"E115.filletArc"),sQuery(id+"F3.wireOp",EDGE,"E116.filletArc"),sQuery(id+"F3.wireOp",EDGE,"E117.filletArc"),sQuery(id+"F3.wireOp",EDGE,"E118.filletArc")])],"isStart":true})]});
            var Q23;
            Q23=makeQuery(id+"F8.opFillet","BLEND_EDGE",EDGE,{"blendedFrom":[makeQuery(id+"F7.boolean.opBoolean","COPY",EDGE,{"derivedFrom":makeQuery(id+"F7.opExtrude","CAP_EDGE",EDGE,{"disambiguationData":[OSD([sQuery(id+"F6.wireOp",EDGE,"E120.0.7.1")])],"isStart":false})}),makeQuery(id+"F4.opExtrude","CAP_FACE",FACE,{"disambiguationData":[OSD([sQuery(id+"F3.wireOp",EDGE,"E112.bottom"),sQuery(id+"F3.wireOp",EDGE,"E112.top"),sQuery(id+"F3.wireOp",EDGE,"E112.left"),sQuery(id+"F3.wireOp",EDGE,"E112.right"),sQuery(id+"F3.wireOp",EDGE,"E113.bottom"),sQuery(id+"F3.wireOp",EDGE,"E113.left"),sQuery(id+"F3.wireOp",EDGE,"E113.right"),sQuery(id+"F3.wireOp",EDGE,"E114.trimOffspring"),sQuery(id+"F3.wireOp",EDGE,"E115.filletArc"),sQuery(id+"F3.wireOp",EDGE,"E116.filletArc"),sQuery(id+"F3.wireOp",EDGE,"E117.filletArc"),sQuery(id+"F3.wireOp",EDGE,"E118.filletArc")])],"isStart":true})],"blendedInto":[makeQuery(id+"F4.opExtrude","CAP_FACE",FACE,{"disambiguationData":[OSD([sQuery(id+"F3.wireOp",EDGE,"E112.bottom"),sQuery(id+"F3.wireOp",EDGE,"E112.top"),sQuery(id+"F3.wireOp",EDGE,"E112.left"),sQuery(id+"F3.wireOp",EDGE,"E112.right"),sQuery(id+"F3.wireOp",EDGE,"E113.bottom"),sQuery(id+"F3.wireOp",EDGE,"E113.left"),sQuery(id+"F3.wireOp",EDGE,"E113.right"),sQuery(id+"F3.wireOp",EDGE,"E114.trimOffspring"),sQuery(id+"F3.wireOp",EDGE,"E115.filletArc"),sQuery(id+"F3.wireOp",EDGE,"E116.filletArc"),sQuery(id+"F3.wireOp",EDGE,"E117.filletArc"),sQuery(id+"F3.wireOp",EDGE,"E118.filletArc")])],"isStart":true})]});
            fillet(context, id + "F9", {"entities" : qUnion([Q0, Q1, Q2, Q3, Q4, Q5, Q6, Q7, Q8, Q9, Q10, Q11, Q12, Q13, Q14, Q15, Q16, Q17, Q18, Q19, Q20, Q21, Q22, Q23]), "radius" : 2 * mm, "tangentPropagation" : true, "allowEdgeOverflow" : false});
        }
        {
            var Q0;
            {var subQ6=sQuery(id+"F0.wireOp",EDGE,"E0.top");Q0=makeQuery(id+"F0.imprint","IMPRINT",FACE,{"disambiguationData":[TD([[makeQuery(id+"F0.imprint","IMPRINT",EDGE,{"derivedFrom":subQ6}),-1.0]])]});}
            var sketch = newSketch(context, id + "F10", { "sketchPlane" : qUnion([Q0])});
            skLineSegment(sketch, "E121.bottom", {"start": v(-490, 1810) * mm, "end": v(910, 1810) * mm});
            skLineSegment(sketch, "E121.top", {"start": v(-490, 1190) * mm, "end": v(910, 1190) * mm});
            skLineSegment(sketch, "E121.left", {"start": v(-490, 1810) * mm, "end": v(-490, 1190) * mm});
            skLineSegment(sketch, "E121.right", {"start": v(910, 1810) * mm, "end": v(910, 1190) * mm});
            skSolve(sketch);
        }
        {
            var Q0;
            Q0 = qSketchRegion(id + "F10", true);
            extrude(context, id + "F11", {"entities" : qUnion([Q0]), "depth" : 30 * mm, "offsetDistance" : 25 * mm});
        }
        {
            var Q0;
            Q0=makeQuery(id+"F11.opExtrude","CAP_FACE",FACE,{"disambiguationData":[OSD([sQuery(id+"F10.wireOp",EDGE,"E121.bottom"),sQuery(id+"F10.wireOp",EDGE,"E121.top"),sQuery(id+"F10.wireOp",EDGE,"E121.left"),sQuery(id+"F10.wireOp",EDGE,"E121.right")])],"isStart":false});
            var sketch = newSketch(context, id + "F12", { "sketchPlane" : qUnion([Q0])});
            skLineSegment(sketch, "E122.bottom", {"start": v(-295, 1190) * mm, "end": v(465, 1190) * mm});
            skLineSegment(sketch, "E122.top", {"start": v(-270, 1670) * mm, "end": v(440, 1670) * mm});
            skLineSegment(sketch, "E122.left", {"start": v(-295, 1190) * mm, "end": v(-295, 1645) * mm});
            skLineSegment(sketch, "E122.right", {"start": v(465, 1190) * mm, "end": v(465, 1645) * mm});
            skPoint(sketch, "E123.visualSharp", {"position": v(-295, 1670) * mm});
            skArc(sketch, "E123.filletArc", {"start": v(-270, 1670) * mm, "mid": v(-287.68, 1662.68) * mm, "end": v(-295, 1645) * mm});
            skPoint(sketch, "E124.visualSharp", {"position": v(465, 1670) * mm});
            skArc(sketch, "E124.filletArc", {"start": v(465, 1645) * mm, "mid": v(457.68, 1662.68) * mm, "end": v(440, 1670) * mm});
            skSolve(sketch);
        }
        {
            var Q0;
            Q0 = qSketchRegion(id + "F12", true);
            extrude(context, id + "F13", {"entities" : qUnion([Q0]), "operationType" : NewBodyOperationType.REMOVE, "oppositeDirection" : true, "depth" : 30 * mm, "offsetDistance" : 25 * mm});
        }
        {
            var Q0;
            Q0=makeQuery(id+"F13.boolean.opBoolean","COPY",EDGE,{"derivedFrom":makeQuery(id+"F13.opExtrude","SWEPT_EDGE",EDGE,{"disambiguationData":[OSD([sQuery(id+"F10.wireOp",EDGE,"E121.top"),sQuery(id+"F12.wireOp",EDGE,"E122.bottom"),sQuery(id+"F12.wireOp",EDGE,"E122.left")])]})});
            var Q1;
            Q1=makeQuery(id+"F13.boolean.opBoolean","COPY",EDGE,{"derivedFrom":makeQuery(id+"F13.opExtrude","SWEPT_EDGE",EDGE,{"disambiguationData":[OSD([sQuery(id+"F10.wireOp",EDGE,"E121.top"),sQuery(id+"F12.wireOp",EDGE,"E122.bottom"),sQuery(id+"F12.wireOp",EDGE,"E122.right")])]})});
            fillet(context, id + "F14", {"entities" : qUnion([Q0, Q1]), "radius" : 25 * mm, "tangentPropagation" : true, "allowEdgeOverflow" : false});
        }
    });
